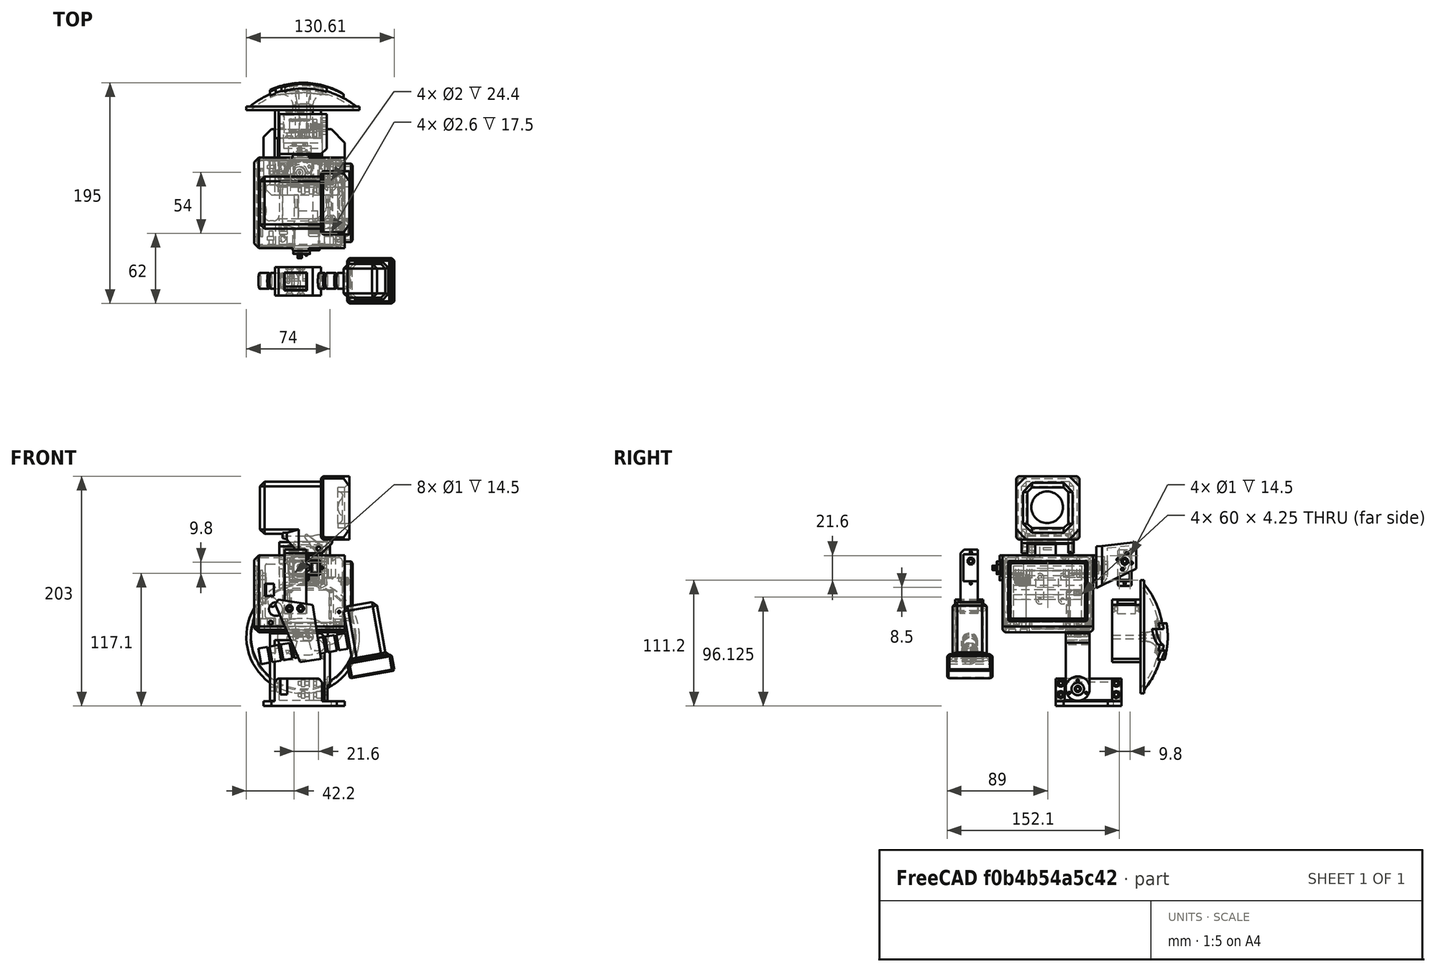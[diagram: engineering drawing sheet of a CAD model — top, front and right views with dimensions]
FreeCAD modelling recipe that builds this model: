
FCSTD DOCUMENT  (FreeCAD 0.16R6348 (Git))
Label: zowi
License: CC-BY 3.0
LicenseURL: http://creativecommons.org/licenses/by/3.0/
objects: Part::Feature×191, Part::Cut×73, Part::Cylinder×67, Part::MultiFuse×58, Part::Box×55, Part::FeaturePython×27, App::DocumentObjectGroup×25, Sketcher::SketchObject×24, Part::Chamfer×21, App::Annotation×20, Part::Fillet×16, PartDesign::Pad×15, Part::Mirroring×13, Part::Part2DObjectPython×11, Part::Sphere×6, PartDesign::Pocket×6, Part::Prism×5, PartDesign::Fillet×3, PartDesign::Chamfer×3, PartDesign::Revolution×3, +3 more types
note: 625 computed .brp shape members not serialized (recipe doc carries the construction recipe); baked Part::Feature solids carry a one-line shape summary decoded from their .brp

FEATURE [Part::Feature] Part__Feature013  label="Servo-D1"
  Placement = pos=(26.5,9.5,100.6) rot=(0,1,0;3.14159rad)
  shape: bbox 55.5 x 20 x 41.74 mm, 365 faces (baked)
FEATURE [Part::Feature] Part__Feature014  label="Servo-D2"
  Placement = pos=(0,0,13) rot=(0.57735,0.57735,0.57735;2.0944rad)
  shape: bbox 41.74 x 55.5 x 20 mm, 365 faces (baked)
FEATURE [Part::Feature] Part__Feature008  label="J1"
  Placement = pos=(-10.8,44.37,77.54) rot=(0.707107,0.707107,0;3.14159rad)
  shape: bbox 11.7 x 15.49 x 2.5 mm, 224 faces (baked)
FEATURE [Part::Feature] Part__Feature009  label="J2"
  Placement = pos=(-10.8,62.15,77.54) rot=(0.707107,0.707107,0;3.14159rad)
  shape: bbox 11.7 x 15.49 x 2.5 mm, 224 faces (baked)
FEATURE [Part::Feature] Part__Feature007  label="J4"
  Placement = pos=(-10.8,59.6199,125.78) rot=(0,0,-1;1.5708rad)
  shape: bbox 11.65 x 20.57 x 2.5 mm, 290 faces (baked)
FEATURE [Part::Feature] Part__Feature010  label="J16"
  Placement = pos=(-9.55,7.19908,100.417) rot=(0.57735,0.57735,-0.57735;2.0944rad)
  shape: bbox 2.94 x 5.43 x 7.98 mm, 414 faces, 0 solids (baked)
FEATURE [Part::Feature] Part__Feature005  label="PCB"
  Placement = pos=(-12.3914,5,75) rot=(0.57735,0.57735,0.57735;2.0944rad)
  shape: bbox 1.591 x 68.6 x 53.36 mm, 426 faces (baked)
FEATURE [Part::Feature] Part__Feature004  label="J010"
  Placement = pos=(-10.8,14.8841,83.3059) rot=(0.707107,0.707107,0;3.14159rad)
  shape: bbox 10.92 x 14.61 x 8.89 mm, 41 faces (baked)
FEATURE [Part::Feature] Part__Feature011  label="U1"
  Placement = pos=(-9.2,12.159,115.511) rot=(0.57735,-0.57735,-0.57735;2.0944rad)
  shape: bbox 2.435 x 26.9 x 13 mm, 503 faces (baked)
FEATURE [Part::Feature] Part__Feature006  label="J8"
  Placement = pos=(-10.8,37.7759,125.78) rot=(0,0,-1;1.5708rad)
  shape: bbox 11.65 x 20.57 x 2.5 mm, 290 faces (baked)
FEATURE [App::DocumentObjectGroup] Group001  label="placa"
  Group = -> [Part__Feature008,Part__Feature009,Part__Feature007,Part__Feature010,Part__Feature005,Part__Feature004,Part__Feature011,Part__Feature006]
FEATURE [Part::Box] Box  label="Cube"
  Height = 24
  Length = 72
  Placement = pos=(-15,-29,-3) rot=(0,0,1;0rad)
  Width = 58
FEATURE [Part::Box] Box001  label="Cube001"
  Height = 25
  Length = 47
  Placement = pos=(-1,-21,2) rot=(0,0,1;0rad)
  Width = 42
FEATURE [Part::Box] Box002  label="Cube002"
  Height = 38
  Length = 28
  Placement = pos=(37,-45,1) rot=(0,0,1;0rad)
  Width = 88
FEATURE [Part::Box] Box003  label="Cube003"
  Height = 38
  Length = 28
  Placement = pos=(-33,-45,1) rot=(0,0,1;0rad)
  Width = 88
FEATURE [Part::Cut] Cut
  Base = -> Box
  Tool = -> Box001
FEATURE [Part::Cut] Cut001
  Base = -> Cut
  Tool = -> Box002
FEATURE [Part::Cut] Cut002
  Base = -> Cut001
  Tool = -> Box003
FEATURE [Part::Box] Box004  label="Cube004"
  Height = 60
  Length = 44
  Placement = pos=(-5,-24,-5) rot=(0,0,1;0rad)
  Width = 61
FEATURE [Part::Mirroring] Part__Mirroring  label="Servo-D1 (Mirror #1)"
  Base = (0,0,0)
  Normal = (0,1,0)
  Placement = pos=(0,72,0) rot=(0,0,1;0rad)
  Source = -> Part__Feature013
FEATURE [Part::Mirroring] Part__Mirroring001  label="Servo-D2 (Mirror #2)"
  Base = (0,0,0)
  Normal = (0,1,0)
  Placement = pos=(0,72,0) rot=(0,0,1;0rad)
  Source = -> Part__Feature014
FEATURE [Part::Cylinder] Cylinder003  label="Joint-D005"
  Angle = 360
  Height = 74.5
  Placement = pos=(-22,9.5,12) rot=(0,1,0;1.5708rad)
  Radius = 1.75
FEATURE [Part::Fillet] Fillet
  Base = -> Cut002
  Edges = 4 edges r=10: [Edge1,Edge3,Edge5,Edge14]
FEATURE [Part::Cylinder] Cylinder002  label="Joint-D004"
  Angle = 360
  Height = 53
  Placement = pos=(-9,9.5,12) rot=(0,1,0;1.5708rad)
  Radius = 10.5
FEATURE [Part::MultiFuse] Fusion
  Shapes = -> [Cylinder002]
FEATURE [Part::Cylinder] Cylinder004  label="Joint-D006"
  Angle = 360
  Height = 74.5
  Placement = pos=(16,9.5,12) rot=(0,1,0;1.5708rad)
  Radius = 5.5
FEATURE [Part::Cut] Cut003
  Base = -> Fusion
  Tool = -> Box004
FEATURE [Part::Cylinder] Cylinder005  label="Joint-D007"
  Angle = 360
  Height = 74.5
  Placement = pos=(-51,9.5,12) rot=(0,1,0;1.5708rad)
  Radius = 1.75
FEATURE [Part::Cut] Cut004
  Base = -> Cut003
  Tool = -> Cylinder004
FEATURE [Part::Cut] Cut005
  Base = -> Cut004
  Tool = -> Cylinder005
FEATURE [Part::Cylinder] Cylinder006  label="Joint-D008"
  Angle = 360
  Height = 74.5
  Placement = pos=(41.8,9.5,12) rot=(0,1,0;1.5708rad)
  Radius = 11
FEATURE [Part::Cut] Cut006
  Base = -> Cut005
  Tool = -> Cylinder006
FEATURE [Part::Cylinder] Cylinder007  label="Joint-D009"
  Angle = 360
  Height = 23.5
  Placement = pos=(16.8,9.5,58.3) rot=(0,1,0;3.14159rad)
  Radius = 11
FEATURE [Part::Cylinder] Cylinder008  label="Joint-D010"
  Angle = 360
  Height = 21.5
  Placement = pos=(16,-24.5,7) rot=(0,1,0;1.5708rad)
  Radius = 1.75
FEATURE [Part::Cylinder] Cylinder009  label="Joint-D011"
  Angle = 360
  Height = 21.5
  Placement = pos=(32,-24.5,7) rot=(0,1,0;1.5708rad)
  Radius = 3
FEATURE [Part::MultiFuse] Fusion001
  Shapes = -> [Cylinder009,Cylinder008]
FEATURE [Part::MultiFuse] Fusion002
  Placement = pos=(0,0,10) rot=(0,0,1;0rad)
  Shapes = -> [Cylinder009,Cylinder008]
FEATURE [Part::MultiFuse] Fusion003
  Placement = pos=(0,49,0) rot=(0,0,1;0rad)
  Shapes = -> [Cylinder009,Cylinder008]
FEATURE [Part::MultiFuse] Fusion004
  Placement = pos=(0,49,10) rot=(0,0,1;0rad)
  Shapes = -> [Cylinder009,Cylinder008]
FEATURE [Part::Box] Box006  label="Cube006"
  Height = 21
  Length = 4
  Placement = pos=(25.5,-28,2) rot=(0,0,1;0rad)
  Width = 56
FEATURE [Part::Cylinder] Cylinder010  label="Joint-D012"
  Angle = 360
  Height = 74.5
  Placement = pos=(17,9.5,12) rot=(0,0,1;0rad)
  Radius = 5.5
FEATURE [Part::Box] Box007  label="Cube007"
  Height = 6
  Length = 3
  Placement = pos=(18.5,-28,4) rot=(0,0,1;0rad)
  Width = 56
FEATURE [Part::Box] Box008  label="Cube008"
  Height = 6
  Length = 3
  Placement = pos=(18.5,-28,14) rot=(0,0,1;0rad)
  Width = 56
FEATURE [Part::Cylinder] Cylinder011  label="Joint-D013"
  Angle = 360
  Height = 74.5
  Placement = pos=(-3,9.5,12) rot=(0,1,0;1.5708rad)
  Radius = 2.75
FEATURE [Part::Box] Box009  label="Cube009"
  Height = 5
  Length = 80
  Placement = pos=(-23,-4,63) rot=(0,0,1;0rad)
  Width = 80
FEATURE [Part::Box] Box010  label="Cube010"
  Height = 9
  Length = 7
  Placement = pos=(-1,-1,63) rot=(0,0,1;0rad)
  Width = 74
FEATURE [Part::Box] Box011  label="Cube011"
  Height = 9
  Length = 7
  Placement = pos=(47,-1,63) rot=(0,0,1;0rad)
  Width = 74
FEATURE [Part::MultiFuse] Fusion005
  Placement = pos=(44,39,98) rot=(0,1,0;1.5708rad)
  Shapes = -> [Cylinder009,Cylinder008]
FEATURE [Part::MultiFuse] Fusion008
  Placement = pos=(44,29,98) rot=(0,1,0;1.5708rad)
  Shapes = -> [Cylinder009,Cylinder008]
FEATURE [Part::MultiFuse] Fusion009
  Placement = pos=(-5,39,98) rot=(0,1,0;1.5708rad)
  Shapes = -> [Cylinder009,Cylinder008]
FEATURE [Part::MultiFuse] Fusion010
  Placement = pos=(-5,29,98) rot=(0,1,0;1.5708rad)
  Shapes = -> [Cylinder009,Cylinder008]
FEATURE [Part::Box] Box012  label="Cube012"
  Height = 9
  Length = 70
  Placement = pos=(-6,8.5,70) rot=(0,0,1;0rad)
  Width = 2
FEATURE [Part::MultiFuse] Fusion011
  Shapes = -> [Box012,Fusion009,Fusion010,Fusion008,Fusion005]
FEATURE [Part::MultiFuse] Fusion012
  Placement = pos=(0,53,0) rot=(0,0,1;0rad)
  Shapes = -> [Box012,Fusion009,Fusion010,Fusion008,Fusion005]
FEATURE [Part::MultiFuse] Fusion013
  Shapes = -> [Box009,Box011,Box010]
FEATURE [Part::Cut] Cut018
  Base = -> Fusion013
  Tool = -> Fusion012
FEATURE [Part::Cut] Cut019
  Base = -> Cut018
  Tool = -> Fusion011
FEATURE [Part::Box] Box014  label="Cube014"
  Height = 43
  Length = 41
  Placement = pos=(6,-1,59) rot=(0,0,1;0rad)
  Width = 21
FEATURE [Part::Box] Box015  label="Cube015"
  Height = 43
  Length = 41
  Placement = pos=(6,52,59) rot=(0,0,1;0rad)
  Width = 21
FEATURE [Part::Cut] Cut020
  Base = -> Cut019
  Tool = -> Box014
FEATURE [Part::Cut] Cut021
  Base = -> Cut020
  Tool = -> Box015
FEATURE [Part::Box] Box016  label="Cube016"
  Height = 12
  Length = 6
  Placement = pos=(-11.5,3,69) rot=(0,0,1;0rad)
  Width = 3
FEATURE [Part::Box] Box017  label="Cube017"
  Height = 12
  Length = 16
  Placement = pos=(-20,-1,63) rot=(0,0,1;0rad)
  Width = 74
FEATURE [Part::Box] Box018  label="Cube018"
  Height = 12
  Length = 6
  Placement = pos=(-11.5,66,69) rot=(0,0,1;0rad)
  Width = 3
FEATURE [Part::MultiFuse] Fusion014
  Shapes = -> [Cut021,Box017]
FEATURE [Part::Cut] Cut022
  Base = -> Fusion014
  Tool = -> Box016
FEATURE [Part::Cut] Cut023
  Base = -> Cut022
  Tool = -> Box018
FEATURE [Part::Box] Box019  label="Cube019"
  Height = 66
  Length = 76
  Placement = pos=(-21,-2,87) rot=(0,0,1;0rad)
  Width = 76
FEATURE [Part::Fillet] Fillet006
  Base = -> Box019
  Edges = 8 edges r=3.5: [Edge1,Edge2,Edge3,Edge5,Edge6,Edge7,Edge10,Edge12]
  Placement = pos=(0,0,-24) rot=(0,0,1;0rad)
FEATURE [Part::Cylinder] Cylinder014  label="Cylinder002"
  Angle = 360
  Height = 31
  Placement = pos=(-8.5,11,71.5) rot=(1,0,0;1.5708rad)
  Radius = 1.75
FEATURE [Part::Cylinder] Cylinder015  label="Cylinder003"
  Angle = 360
  Height = 31
  Placement = pos=(-8.5,80,71.5) rot=(1,0,0;1.5708rad)
  Radius = 1.75
FEATURE [Part::Cylinder] Cylinder016  label="Cylinder004"
  Angle = 360
  Height = 31
  Placement = pos=(-4,11,83.5) rot=(1,0,0;1.5708rad)
  Radius = 6
FEATURE [Part::Box] Box020  label="Cube020"
  Height = 11
  Length = 8
  Placement = pos=(-13.5,-13,95) rot=(0,0,1;0rad)
  Width = 24
FEATURE [PartDesign::Fillet] Fillet011  label="horn"
  Placement = pos=(38.5,9.5,13) rot=(0,0,-1;1.5708rad)
  Radius = 0.5
FEATURE [Part::Cylinder] Cylinder021  label="Joint-D014"
  Angle = 360
  Height = 52.5
  Placement = pos=(19,9.5,20.35) rot=(0,1,0;1.5708rad)
  Radius = 1
FEATURE [Part::Cylinder] Cylinder022  label="Joint-D015"
  Angle = 360
  Height = 52.5
  Placement = pos=(19,2,9.5) rot=(0,1,0;1.5708rad)
  Radius = 1
FEATURE [Part::Cylinder] Cylinder023  label="Joint-D016"
  Angle = 360
  Height = 52.5
  Placement = pos=(19,17,9.5) rot=(0,1,0;1.5708rad)
  Radius = 1
FEATURE [Part::MultiFuse] Fusion017
  Placement = pos=(0,0,-1) rot=(0,0,1;0rad)
  Shapes = -> [Cylinder022,Cylinder021,Cylinder023]
FEATURE [Part::MultiFuse] Fusion018
  Placement = pos=(4,0,101) rot=(0,1,0;1.5708rad)
  Shapes = -> [Cylinder022,Cylinder021,Cylinder023]
FEATURE [PartDesign::Fillet] Fillet012  label="horn001"
  Placement = pos=(16.8,9.5,62.5) rot=(-0.57735,0.57735,-0.57735;2.0944rad)
  Radius = 0.5
FEATURE [Part::Mirroring] Part__Mirroring003  label="horn (Mirror #4)"
  Base = (41.6,1.90735e-06,13)
  Normal = (0,1,-1.19209e-07)
  Placement = pos=(0,72,0) rot=(0,0,1;0rad)
  Source = -> Fillet011
FEATURE [Part::Mirroring] Part__Mirroring004  label="horn001 (Mirror #5)"
  Base = (16.8,7.62939e-06,59.3998)
  Normal = (0,1,-1.19209e-07)
  Placement = pos=(0,72,0) rot=(0,0,1;0rad)
  Source = -> Fillet012
FEATURE [Part::Chamfer] Chamfer
  Base = -> Fillet
  Edges = 3 edges r=3: [Edge18,Edge33,Edge37]
FEATURE [Part::Cut] Cut008
  Base = -> Chamfer
  Tool = -> Cylinder003
FEATURE [Part::Cut] Cut010
  Base = -> Cut008
  Tool = -> Box006
FEATURE [Part::Cut] Cut011
  Base = -> Cut010
  Tool = -> Box008
FEATURE [Part::Cut] Cut012
  Base = -> Cut011
  Tool = -> Box007
FEATURE [Part::Cut] Cut013
  Base = -> Cut012
  Tool = -> Fusion004
FEATURE [Part::Cut] Cut014
  Base = -> Cut013
  Tool = -> Fusion003
FEATURE [Part::Cut] Cut015
  Base = -> Cut014
  Tool = -> Fusion002
FEATURE [Part::Cut] Cut016
  Base = -> Cut015
  Tool = -> Fusion001
FEATURE [Part::Cut] Cut017  label="pie"
  Base = -> Cut016
  Tool = -> Cylinder011
FEATURE [Part::Box] Box024  label="Cube024"
  Height = 23
  Length = 6
  Placement = pos=(0,19,7) rot=(0,0,1;0rad)
  Width = 36
FEATURE [Part::Cut] Cut039  label="pie-D"
  Base = -> Cut017
  Placement = pos=(0,0,1) rot=(0,0,1;0rad)
  Tool = -> Box024
FEATURE [Part::Mirroring] Part__Mirroring006  label="pie-I"
  Base = (0,0,0)
  Normal = (0,1,0)
  Placement = pos=(0,72,0) rot=(0,0,1;0rad)
  Source = -> Cut039
FEATURE [Part::Cut] Cut044
  Base = -> Cut006
  Tool = -> Box004
FEATURE [Part::Cut] Cut045
  Base = -> Cut044
  Tool = -> Cylinder007
FEATURE [Part::Cut] Cut046
  Base = -> Cut045
  Tool = -> Fusion018
FEATURE [Part::Cut] Cut047
  Base = -> Cut046
  Tool = -> Fusion017
FEATURE [Part::Cut] Cut048
  Base = -> Cut047
  Placement = pos=(0,0,1) rot=(0,0,1;0rad)
  Tool = -> Cylinder010
FEATURE [Part::Chamfer] Chamfer001
  Base = -> Cut048
  Edges = 1 edges r=4: [Edge61]
FEATURE [Part::Chamfer] Chamfer002  label="pata-D"
  Base = -> Chamfer001
  Edges = 1 edges r=8: [Edge58]
FEATURE [Part::Mirroring] Part__Mirroring007  label="pata-I"
  Base = (17.5,3.8147e-06,32.25)
  Normal = (0,1,-1.19209e-07)
  Placement = pos=(0,72,0) rot=(0,0,1;0rad)
  Source = -> Chamfer002
FEATURE [Part::Cylinder] Cylinder026  label="Cylinder029"
  Angle = 360
  Height = 31
  Placement = pos=(-7,80,89.6) rot=(1,0,0;1.5708rad)
  Radius = 4
FEATURE [Part::Cylinder] Cylinder012  label="Cylinder030"
  Angle = 360
  Height = 31
  Placement = pos=(-8.5,92,71.5) rot=(1,0,0;1.5708rad)
  Radius = 1.75
FEATURE [Part::Cut] Cut024
  Base = -> Cut023
  Tool = -> Cylinder012
FEATURE [Part::Cylinder] Cylinder013  label="Cylinder001"
  Angle = 360
  Height = 31
  Placement = pos=(-8.5,11,71.5) rot=(1,0,0;1.5708rad)
  Radius = 1.75
FEATURE [Part::Feature] Part__Feature  label="Portapilas008"
  shape: bbox 2e-07 x 47.97 x 51.59 mm, 1 faces, 0 solids (baked)
FEATURE [Part::Feature] Part__Feature015  label="Portapilas007"
  shape: bbox 9.213 x 1.1 x 48.01 mm, 3 faces, 0 solids (baked)
FEATURE [Part::Feature] Part__Feature016  label="Portapilas006"
  shape: bbox 9.213 x 1.1 x 48.01 mm, 3 faces, 0 solids (baked)
FEATURE [Part::Feature] Part__Feature017  label="Portapilas005"
  shape: bbox 9.213 x 1.1 x 48.01 mm, 3 faces, 0 solids (baked)
FEATURE [Part::Feature] Part__Feature018  label="Portapilas004"
  shape: bbox 9.213 x 1.1 x 48.01 mm, 3 faces, 0 solids (baked)
FEATURE [Part::Feature] Part__Feature019  label="Portapilas003"
  shape: bbox 9.213 x 1.1 x 48.01 mm, 3 faces, 0 solids (baked)
FEATURE [Part::Feature] Part__Feature020  label="Portapilas002"
  shape: bbox 9.213 x 1.1 x 48.01 mm, 3 faces, 0 solids (baked)
FEATURE [Part::Feature] Part__Feature021  label="Portapilas001"
  shape: bbox 16.42 x 48.04 x 51.59 mm, 26 faces, 0 solids (baked)
FEATURE [Part::Feature] Part__Feature022  label="Portapilas"
  shape: bbox 21.03 x 69.14 x 72.63 mm, 394 faces, 0 solids (baked)
FEATURE [Part::MultiFuse] Fusion019  label="peterpilas"
  Placement = pos=(23,77.5,76) rot=(0,0,1;1.5708rad)
  Shapes = -> [Part__Feature022,Part__Feature021,Part__Feature020,Part__Feature019,Part__Feature018,Part__Feature017,Part__Feature016,Part__Feature015,Part__Feature]
FEATURE [Part::Feature] Part__Feature023  label="Ultrasonido_BAT"
  Placement = pos=(-17,36,59.5) rot=(0,0,1;0rad)
  shape: bbox 18.72 x 56 x 27.52 mm, 81 faces (baked)
FEATURE [Part::Cylinder] Cylinder027  label="Joint-D019"
  Angle = 360
  Height = 24
  Placement = pos=(16.8,9.5,81) rot=(0,1,0;3.14159rad)
  Radius = 10
FEATURE [Part::Cylinder] Cylinder028  label="Joint-D020"
  Angle = 360
  Height = 24
  Placement = pos=(4.8,9.5,13) rot=(0,1,0;1.5708rad)
  Radius = 10
FEATURE [Part::Mirroring] Part__Mirroring008  label="Joint-D019 (Mirror #7)"
  Base = (0,0,0)
  Normal = (0,1,0)
  Placement = pos=(0,72,0) rot=(0,0,1;0rad)
  Source = -> Cylinder027
FEATURE [Part::Mirroring] Part__Mirroring009  label="Joint-D020 (Mirror #8)"
  Base = (22,1.90735e-06,13)
  Normal = (0,1,-1.19209e-07)
  Placement = pos=(0,72,0) rot=(0,0,1;0rad)
  Source = -> Cylinder028
FEATURE [Part::Box] Box031  label="Cube031"
  Height = 4
  Length = 72
  Placement = pos=(-15,-29,-2) rot=(0,0,1;0rad)
  Width = 58
FEATURE [Part::Fillet] Fillet025
  Base = -> Box031
  Edges = 4 edges r=10: [Edge1,Edge3,Edge5,Edge7]
FEATURE [Part::Mirroring] Part__Mirroring010  label="Fillet025 (Mirror #9)"
  Base = (0,0,0)
  Normal = (0,1,0)
  Placement = pos=(0,72,0) rot=(0,0,1;0rad)
  Source = -> Fillet025
FEATURE [Part::Cylinder] Cylinder034  label="Cylinder082"
  Angle = 360
  Height = 35
  Placement = pos=(51.6,9.5,33) rot=(0.707107,0,-0.707107;3.14159rad)
  Radius = 2.5
FEATURE [Part::Cylinder] Cylinder035  label="Cylinder083"
  Angle = 360
  Height = 20
  Placement = pos=(51.6,9.5,13) rot=(0,0,1;3.14159rad)
  Radius = 2.5
FEATURE [Part::Cylinder] Cylinder036  label="Cylinder084"
  Angle = 360
  Height = 61
  Placement = pos=(-9.4,9.5,13) rot=(0.707107,0,0.707107;3.14159rad)
  Radius = 2.5
FEATURE [Part::Sphere] Sphere
  Angle1 = -90
  Angle2 = 90
  Angle3 = 360
  Placement = pos=(16.8,9.5,33) rot=(1,0,0;3.14159rad)
  Radius = 2.5
FEATURE [Part::Sphere] Sphere008
  Angle1 = -90
  Angle2 = 90
  Angle3 = 360
  Placement = pos=(51.6,9.5,33) rot=(0.707107,0,-0.707107;3.14159rad)
  Radius = 2.5
FEATURE [Part::Cylinder] Cylinder037  label="Cylinder085"
  Angle = 360
  Height = 11
  Placement = pos=(-9.4,9.5,2) rot=(0,0,1;3.14159rad)
  Radius = 2.5
FEATURE [Part::Sphere] Sphere009
  Angle1 = -90
  Angle2 = 90
  Angle3 = 360
  Placement = pos=(51.6,9.5,13) rot=(0.707107,0,-0.707107;3.14159rad)
  Radius = 2.5
FEATURE [Part::Cylinder] Cylinder038  label="cylinder001"
  Angle = 360
  Height = 83
  Placement = pos=(16.8,9.5,33) rot=(0,0,1;3.14159rad)
  Radius = 2.5
FEATURE [Part::Sphere] Sphere010
  Angle1 = -90
  Angle2 = 90
  Angle3 = 360
  Placement = pos=(16.8,9.5,116) rot=(1,0,0;3.14159rad)
  Radius = 2.5
FEATURE [Part::Sphere] Sphere011
  Angle1 = -90
  Angle2 = 90
  Angle3 = 360
  Placement = pos=(-9.4,9.5,2) rot=(0.707107,0,-0.707107;3.14159rad)
  Radius = 2.5
FEATURE [Part::Sphere] Sphere012
  Angle1 = -90
  Angle2 = 90
  Angle3 = 360
  Placement = pos=(-9.4,9.5,13) rot=(0.707107,0,-0.707107;3.14159rad)
  Radius = 2.5
FEATURE [Part::Cylinder] Cylinder039  label="Cylinder086"
  Angle = 360
  Height = 53
  Placement = pos=(16.8,9.5,116) rot=(-1,0,0;1.5708rad)
  Radius = 2.5
FEATURE [Part::MultiFuse] Fusion021
  Placement = pos=(0,53,0) rot=(0,0,1;0rad)
  Shapes = -> [Cylinder037,Cylinder036,Sphere012,Cylinder035,Cylinder034,Cylinder038,Sphere010,Sphere008,Sphere009,Sphere,Sphere011]
FEATURE [Part::MultiFuse] Fusion022
  Shapes = -> [Cylinder037,Cylinder036,Sphere012,Cylinder035,Cylinder034,Cylinder038,Sphere010,Sphere008,Sphere009,Sphere,Sphere011]
FEATURE [App::DocumentObjectGroup] Group  label="kinematic"
  Group = -> [Cylinder039,Part__Mirroring008,Cylinder027,Fusion021,Fusion022,Cylinder028,Part__Mirroring009,Part__Mirroring010,Fillet025]
FEATURE [Part::Cut] Cut050
  Base = -> Cut024
  Tool = -> Cylinder013
FEATURE [Part::Box] Box032  label="Cube032"
  Height = 25
  Length = 55
  Placement = pos=(-1,20,66) rot=(0,0,1;0rad)
  Width = 32
FEATURE [Part::Box] Box033  label="Cube033"
  Height = 54
  Length = 4.5
  Placement = pos=(-20,6,64) rot=(0,0,1;0rad)
  Width = 60
FEATURE [Part::Box] Box035  label="Cube035"
  Height = 68
  Length = 6
  Placement = pos=(-23.5,17,68) rot=(0,0,1;0rad)
  Width = 38
FEATURE [Part::Box] Box036  label="Cube034"
  Height = 17
  Length = 13
  Placement = pos=(-14,20,62) rot=(0,0,1;0rad)
  Width = 32
FEATURE [Part::Fillet] Fillet018002
  Base = -> Box036
  Edges = 4 edges r=5: [Edge1,Edge3,Edge5,Edge7]
FEATURE [Part::Cylinder] Cylinder  label="Cylinder087"
  Angle = 360
  Height = 31
  Placement = pos=(-49.5,29,111.5) rot=(0,1,0;1.5708rad)
  Radius = 1.75
FEATURE [Part::Cylinder] Cylinder040  label="Cylinder088"
  Angle = 360
  Height = 31
  Placement = pos=(-49.5,49,91.5) rot=(0,1,0;1.5708rad)
  Radius = 1.75
FEATURE [Part::Cylinder] Cylinder041  label="Cylinder089"
  Angle = 360
  Height = 31
  Placement = pos=(-49.5,49,111.5) rot=(0,1,0;1.5708rad)
  Radius = 1.75
FEATURE [Part::MultiFuse] Fusion025
  Shapes = -> [Box032,Cut050]
FEATURE [Part::Box] Box037  label="Cube036"
  Height = 44
  Length = 61
  Placement = pos=(-9,22,66) rot=(0,0,1;0rad)
  Width = 28
FEATURE [Part::MultiFuse] Fusion026
  Shapes = -> [Fusion025,Box033]
FEATURE [Part::Cut] Cut051
  Base = -> Fusion026
  Tool = -> Fillet018002
FEATURE [Part::Box] Box038  label="Cube037"
  Height = 11
  Length = 8
  Placement = pos=(-11.5,-52,95) rot=(0,0,1;0rad)
  Width = 58
FEATURE [Part::Cylinder] Cylinder042  label="Cylinder090"
  Angle = 360
  Height = 61
  Placement = pos=(-5,124,89.6) rot=(1,0,0;1.5708rad)
  Radius = 4
FEATURE [Part::Cylinder] Cylinder043  label="Cylinder091"
  Angle = 360
  Height = 63
  Placement = pos=(-3,11,83.5) rot=(1,0,0;1.5708rad)
  Radius = 6
FEATURE [Part::Box] Box039  label="Cube038"
  Height = 66
  Length = 76
  Placement = pos=(-21,-2,63) rot=(0,0,1;0rad)
  Width = 76
FEATURE [Part::Cylinder] Cylinder044  label="Cylinder092"
  Angle = 360
  Height = 23
  Placement = pos=(-8.5,1,71.5) rot=(1,0,0;1.5708rad)
  Radius = 1.75
FEATURE [Part::Cylinder] Cylinder045  label="Cylinder093"
  Angle = 360
  Height = 31
  Placement = pos=(-8.5,94,71.5) rot=(1,0,0;1.5708rad)
  Radius = 1.75
FEATURE [Part::Fillet] Fillet018007
  Base = -> Box039
  Edges = 8 edges r=3: [Edge1,Edge2,Edge3,Edge5,Edge6,Edge7,Edge10,Edge12]
FEATURE [Part::Box] Box040  label="Cube039"
  Height = 6
  Length = 81
  Placement = pos=(-23.5,-4.5,63) rot=(0,0,1;0rad)
  Width = 81
FEATURE [Part::Fillet] Fillet018008
  Base = -> Box040
  Edges = 4 edges r=5: [Edge1,Edge3,Edge5,Edge7]
  Placement = pos=(0,0,-1) rot=(0,0,1;0rad)
FEATURE [Part::Cylinder] Cylinder046  label="Cylinder094"
  Angle = 360
  Height = 45
  Placement = pos=(-8.5,-7,71.5) rot=(1,0,0;1.5708rad)
  Radius = 4
FEATURE [Part::Cylinder] Cylinder047  label="Cylinder095"
  Angle = 360
  Height = 45
  Placement = pos=(-8.5,124,71.5) rot=(1,0,0;1.5708rad)
  Radius = 4
FEATURE [Part::MultiFuse] Fusion033
  Shapes = -> [Fillet018007,Fillet018008]
FEATURE [Part::MultiFuse] Fusion034  label="corte-positivo"
  Shapes = -> [Fusion033,Cylinder042,Cylinder047,Cylinder045,Cylinder046,Cylinder043,Box038,Cylinder044]
FEATURE [Part::Feature] hull002
  shape: bbox 10 x 17.12 x 30.33 mm, 240 faces (baked)
FEATURE [Part::Box] Box042  label="Cube041"
  Height = 23
  Length = 6
  Placement = pos=(0,19,7) rot=(0,0,1;0rad)
  Width = 36
FEATURE [Part::Cut] Cut060  label="pie001"
  Base = -> Cut016
  Tool = -> Cylinder011
FEATURE [Part::Cut] Cut059  label="piepatin"
  Base = -> Cut060
  Placement = pos=(0,0,1) rot=(0,0,1;0rad)
  Tool = -> Box042
FEATURE [Part::Cylinder] Cylinder052  label="Cylinder096"
  Angle = 360
  Height = 27
  Placement = pos=(8,-25,17) rot=(1,0,0;1.0472rad)
  Radius = 1.75
FEATURE [Part::MultiFuse] Fusion035
  Shapes = -> [hull002,Cut059]
FEATURE [Part::Prism] prism
  Circumradius = 3.5
  Height = 10
  Placement = pos=(8,-17,12.375) rot=(1,0,0;1.0472rad)
  Polygon = 6
FEATURE [Part::MultiFuse] Fusion036
  Shapes = -> [Cylinder052,prism]
FEATURE [Part::Cut] Cut061  label="patin"
  Base = -> Fusion035
  Tool = -> Fusion036
FEATURE [Part::Box] Box044  label="Cube043"
  Height = 30
  Length = 3
  Placement = pos=(-26,16,70) rot=(0,0,1;0rad)
  Width = 40
FEATURE [Part::Feature] Cut062
  Placement = pos=(-82.5,-7.75,37) rot=(0,1,0;3.14159rad)
  shape: bbox 20 x 20 x 38.5 mm, 2097 faces (baked)
FEATURE [Part::Feature] hull003
  shape: bbox 48 x 3 x 83 mm, 8 faces (baked)
FEATURE [Part::MultiFuse] Fusion037  label="cola"
  Shapes = -> [Box044,hull003,Cut062]
FEATURE [App::DocumentObjectGroup] Group002  label="patines"
  Group = -> [Cut061,Fusion037]
FEATURE [Part::Cylinder] Cylinder053  label="Cylinder097"
  Angle = 360
  Height = 31
  Placement = pos=(-49.5,29,91.5) rot=(0,1,0;1.5708rad)
  Radius = 1.75
FEATURE [Part::MultiFuse] Fusion038
  Placement = pos=(14,0,0) rot=(0,0,1;0rad)
  Shapes = -> [Cylinder053,Cylinder040,Cylinder041,Cylinder]
FEATURE [App::DocumentObjectGroup] Group004  label="electronic"
  Group = -> [Part__Mirroring,Part__Mirroring001,Part__Mirroring003,Part__Mirroring004,Fusion019,Part__Feature023,Group001]
FEATURE [App::DocumentObjectGroup] Group005  label="aux"
  Group = -> [Fusion034]
FEATURE [App::DocumentObjectGroup] Group003  label="original-src"
  Group = -> [Part__Mirroring006,Part__Mirroring007,Group004,Group005]
FEATURE [Part::Cut] Cut066
  Base = -> Cut051
  Tool = -> Box037
FEATURE [Part::Chamfer] Chamfer003
  Base = -> Cut066
  Edges = 1 edges r=3: [Edge1]
FEATURE [Sketcher::SketchObject] Sketch
  Placement = pos=(-22,0,0) rot=(0.57735,-0.57735,-0.57735;2.0944rad)
  sketch-geometry (4):
    g0: ArcOfCircle CenterX=-49 CenterY=111.5 CenterZ=0 NormalX=0 NormalY=0 NormalZ=1 Radius=3.5 StartAngle=9.1497e-08 EndAngle=3.14159
    g1: LineSegment StartX=-52.5 StartY=111.5 StartZ=0 EndX=-52.5 EndY=91.5 EndZ=0
    g2: LineSegment StartX=-45.5 StartY=111.5 StartZ=0 EndX=-45.5 EndY=91.5 EndZ=0
    g3: ArcOfCircle CenterX=-49 CenterY=91.5 CenterZ=0 NormalX=0 NormalY=0 NormalZ=1 Radius=3.5 StartAngle=3.14159 EndAngle=6.28319
  constraints (13):
    c: DistanceX(g-1,g0) = -49
    c: DistanceY(g-1,g0) = 111.5
    c: Radius(g0) = 3.5
    c: Vertical(g1)
    c: Vertical(g2)
    c: Coincident(g1,g0)
    c: Coincident(g2,g0)
    c: Tangent(g2,g0)
    c: Tangent(g1,g0)
    c: Coincident(g3,g1)
    c: Coincident(g3,g2)
    c: Equal(g3,g0)
    c: Distance(g3,g0) = 20
FEATURE [PartDesign::Pad] Pad
  Length = 5
  Length2 = 100
  Placement = pos=(-22,0,0) rot=(0.57735,-0.57735,-0.57735;2.0944rad)
  Reversed = true
  Sketch = -> Sketch
  Type = 0
FEATURE [Part::FeaturePython] Clone  label="Clone of Pad"  # Draft clone (typed FeaturePython)
  Objects = -> [Pad]
  Placement = pos=(-22,-20,0) rot=(0.57735,-0.57735,-0.57735;2.0944rad)
  Scale = (1,1,1)
FEATURE [Part::MultiFuse] Fusion039
  Placement = pos=(4.5,0,0) rot=(0,0,1;0rad)
  Shapes = -> [Pad,Clone]
FEATURE [Part::MultiFuse] Fusion040
  Shapes = -> [Chamfer003,Fusion039]
FEATURE [Part::Cut] Cut067
  Base = -> Fusion040
  Tool = -> Fusion038
FEATURE [Part::Cut] Cut068
  Base = -> Cut067
  Tool = -> Box035
FEATURE [Part::Box] Box047  label="Cube046"
  Height = 49
  Length = 17
  Placement = pos=(-14,-2.5,75) rot=(0,0,1;0rad)
  Width = 77
FEATURE [Part::Fillet] Fillet018014
  Base = -> Box047
  Edges = 12 edges r=2: [Edge1,Edge2,Edge3,Edge4,Edge5,Edge6,Edge7,Edge8,Edge9,Edge10,Edge11,Edge12]
FEATURE [Part::Feature] Part__Mirroring007001  label="pata-orig"
  Placement = pos=(-17,-62,-9.49999) rot=(-1,0,0;1.5708rad)
  shape: bbox 53 x 59.5 x 21 mm, 32 faces (baked)
FEATURE [Sketcher::SketchObject] Sketch001  label="leg-sketch-1"
  Placement = pos=(0,0,0) rot=(0.57735,0.57735,0.57735;2.0944rad)
  sketch-geometry (5):
    g0: LineSegment StartX=-49 StartY=10.5 StartZ=0 EndX=0 EndY=10.5 EndZ=0
    g1: LineSegment StartX=0 StartY=10.5 StartZ=0 EndX=0 EndY=-10.5 EndZ=0
    g2: LineSegment StartX=0 StartY=-10.5 StartZ=0 EndX=-49 EndY=-10.5 EndZ=0
    g3: LineSegment [constr] StartX=-49 StartY=-10.5 StartZ=0 EndX=-49 EndY=10.5 EndZ=0
    g4: ArcOfCircle CenterX=-49 CenterY=0 CenterZ=0 NormalX=0 NormalY=0 NormalZ=1 Radius=10.5 StartAngle=1.5708 EndAngle=4.71239
  constraints (15):
    c: Coincident(g0,g1)
    c: Coincident(g1,g2)
    c: Coincident(g2,g3)
    c: Coincident(g3,g0)
    c: Horizontal(g0)
    c: Horizontal(g2)
    c: Vertical(g1)
    c: Vertical(g3)
    c: PointOnObject(g4,g3)
    c: Coincident(g4,g0)
    c: Coincident(g4,g2)
    c: PointOnObject(g4,g-1)
    c: PointOnObject(g0,g-2)
    c: DistanceX(g0) = 49
    c: DistanceY(g1) = -21
FEATURE [PartDesign::Pad] Pad001  label="leg-block-1"
  Length = 53
  Length2 = 100
  Midplane = true
  Placement = pos=(0,0,0) rot=(0.57735,0.57735,0.57735;2.0944rad)
  Sketch = -> Sketch001
  Type = 0
FEATURE [Sketcher::SketchObject] Sketch002  label="leg-top-sketch"
  ExternalGeometry = -> [Pad001]
  Placement = pos=(0,0,10.5) rot=(0,0,-1;1.5708rad)
  Support = -> Pad001 [Face1]
  sketch-geometry (9):
    g0: LineSegment StartX=64 StartY=21.5 StartZ=0 EndX=10 EndY=21.5 EndZ=0
    g1: LineSegment StartX=6 StartY=17.5 StartZ=0 EndX=6 EndY=-19.5 EndZ=0
    g2: LineSegment StartX=9 StartY=-22.5 StartZ=0 EndX=64 EndY=-22.5 EndZ=0
    g3: LineSegment StartX=64 StartY=-22.5 StartZ=0 EndX=64 EndY=21.5 EndZ=0
    g4: LineSegment StartX=6 StartY=17.5 StartZ=0 EndX=10 EndY=21.5 EndZ=0
    g5: LineSegment [constr] StartX=6 StartY=17.5 StartZ=0 EndX=6 EndY=21.5 EndZ=0
    g6: LineSegment StartX=6 StartY=-19.5 StartZ=0 EndX=9 EndY=-22.5 EndZ=0
    g7: LineSegment [constr] StartX=9 StartY=-22.5 StartZ=0 EndX=6 EndY=-22.5 EndZ=0
    g8: LineSegment [constr] StartX=6 StartY=-22.5 StartZ=0 EndX=6 EndY=-19.5 EndZ=0
  constraints (26):
    c: Coincident(g2,g3)
    c: Coincident(g3,g0)
    c: Horizontal(g0)
    c: Horizontal(g2)
    c: Vertical(g1)
    c: Vertical(g3)
    c: DistanceY(g-3,g5) = -5
    c: DistanceY(g7,g-4) = -4
    c: Angle(g-2,g4) = 2.35619
    c: Coincident(g1,g4)
    c: Coincident(g5,g1)
    c: Vertical(g5)
    c: DistanceY(g1,g7) = -40
    c: DistanceX(g5,g-3) = -6
    c: Coincident(g0,g4)
    c: PointOnObject(g5,g0)
    c: DistanceX(g-3,g0) = 15
    c: Coincident(g2,g6)
    c: Coincident(g7,g2)
    c: Horizontal(g7)
    c: DistanceX(g7) = -3
    c: Coincident(g1,g6)
    c: Coincident(g8,g7)
    c: Coincident(g8,g1)
    c: Equal(g8,g7)
    c: Vertical(g8)
FEATURE [PartDesign::Pocket] Pocket  label="leg-block-2"
  Length = 5
  Placement = pos=(0,0,0) rot=(0.57735,0.57735,0.57735;2.0944rad)
  Sketch = -> Sketch002
  Type = 1
FEATURE [Sketcher::SketchObject] Sketch003  label="ankle-rounded-horn-sketch"
  ExternalGeometry = -> [Pocket]
  Placement = pos=(26.5,0,0) rot=(0.57735,0.57735,0.57735;2.0944rad)
  Support = -> Pocket [Face4]
  sketch-geometry (1):
    g0: Circle CenterX=-49 CenterY=0 CenterZ=0 NormalX=0 NormalY=0 NormalZ=1 Radius=10.75
  constraints (2):
    c: Coincident(g0,g-3)
    c: Radius(g0) = 10.75
FEATURE [PartDesign::Pocket] Pocket001  label="ankle-rounded-horn-cutout"
  Length = 2.2
  Placement = pos=(0,0,0) rot=(0.57735,0.57735,0.57735;2.0944rad)
  Sketch = -> Sketch003
  Type = 0
FEATURE [Sketcher::SketchObject] Sketch004  label="ankle-rear-shaft-drill-sketch"
  ExternalGeometry = -> [Pocket001]
  Placement = pos=(-26.5,0,0) rot=(0.57735,0.57735,-0.57735;4.18879rad)
  Support = -> Pocket001 [Face2]
  sketch-geometry (1):
    g0: Circle CenterX=-49 CenterY=0 CenterZ=0 NormalX=0 NormalY=0 NormalZ=1 Radius=1.75
  constraints (2):
    c: Coincident(g0,g-3)
    c: Radius(g0) = 1.75
FEATURE [PartDesign::Pocket] Pocket002  label="ankle-rear-shaft-drill"
  Length = 0
  Placement = pos=(0,0,0) rot=(0.57735,0.57735,0.57735;2.0944rad)
  Sketch = -> Sketch004
  Type = 2
FEATURE [Sketcher::SketchObject] Sketch005  label="hip-rounded-horn-cutout-sketch"
  Placement = pos=(0,-6,0) rot=(-0.57735,-0.57735,0.57735;4.18879rad)
  Support = -> Pocket002 [Face10]
  sketch-geometry (1):
    g0: Circle CenterX=0 CenterY=0 CenterZ=0 NormalX=0 NormalY=0 NormalZ=1 Radius=11
  constraints (2):
    c: Coincident(g0,g-1)
    c: Radius(g0) = 11
FEATURE [PartDesign::Pocket] Pocket003  label="hip-rounded-horn-cutout"
  Length = 3.3
  Placement = pos=(0,0,0) rot=(0.57735,0.57735,0.57735;2.0944rad)
  Sketch = -> Sketch005
  Type = 0
FEATURE [Sketcher::SketchObject] Sketch006  label="horn-side-chamfer-sketch"
  ExternalGeometry = -> [Pocket003]
  Placement = pos=(0,0,10.5) rot=(0,0,-1;1.5708rad)
  Support = -> Pocket003 [Face1]
  sketch-geometry (3):
    g0: LineSegment StartX=0 StartY=18.5 StartZ=0 EndX=8 EndY=26.5 EndZ=0
    g1: LineSegment StartX=0 StartY=18.5 StartZ=0 EndX=0 EndY=26.5 EndZ=0
    g2: LineSegment StartX=0 StartY=26.5 StartZ=0 EndX=8 EndY=26.5 EndZ=0
  constraints (8):
    c: PointOnObject(g0,g-2)
    c: PointOnObject(g0,g-3)
    c: Angle(g-2,g0) = 2.35619
    c: DistanceY(g-3,g0) = -8
    c: Coincident(g0,g1)
    c: Coincident(g1,g-3)
    c: Coincident(g1,g2)
    c: Coincident(g2,g0)
FEATURE [PartDesign::Pocket] Pocket004  label="horn-side-chamfer"
  Length = 5
  Placement = pos=(0,0,0) rot=(0.57735,0.57735,0.57735;2.0944rad)
  Sketch = -> Sketch006
  Type = 1
FEATURE [Part::Cylinder] Cylinder054  label="servo-shaft-drill"
  Angle = 360
  Height = 20
  Placement = pos=(0,10,0) rot=(1,0,0;1.5708rad)
  Radius = 5.5
FEATURE [Part::Cylinder] Cylinder055  label="servo-horn-small-drill-master"
  Angle = 360
  Height = 20
  Placement = pos=(-3.5,10,7.5) rot=(1,0,0;1.5708rad)
  Radius = 1
FEATURE [Part::FeaturePython] Clone001  label="Clone of servo-horn-small-drill-master"  # Draft clone (typed FeaturePython)
  Objects = -> [Cylinder055]
  Placement = pos=(7.35,10,-2.33815e-06) rot=(1,0,0;1.5708rad)
  Scale = (1,1,1)
FEATURE [Part::FeaturePython] Clone002  label="Clone of servo-horn-small-drill-master001"  # Draft clone (typed FeaturePython)
  Objects = -> [Cylinder055]
  Placement = pos=(-3.5,10,-7.5) rot=(1,0,0;1.5708rad)
  Scale = (1,1,1)
FEATURE [Part::MultiFuse] Fusion041  label="servo-Drills-block1-master"
  Shapes = -> [Clone001,Clone002,Cylinder055,Cylinder054]
FEATURE [Part::FeaturePython] Clone003  label="Clone of servo-Drills-block1-master"  # Draft clone (typed FeaturePython)
  Objects = -> [Fusion041]
  Placement = pos=(22,-49,6.96015e-06) rot=(0,0,1;1.5708rad)
  Scale = (1,1,1)
FEATURE [Part::MultiFuse] Fusion042  label="Servo-horn-drills"
  Shapes = -> [Fusion041,Clone003]
FEATURE [Part::Cut] Cut070  label="Leg"
  Base = -> Pocket004
  Tool = -> Fusion042
FEATURE [App::DocumentObjectGroup] Group007  label="Leg-src"
  Group = -> [Pad001,Pocket,Pocket001,Pocket002,Pocket003,Cut070]
FEATURE [Sketcher::SketchObject] Sketch007
  sketch-geometry (15):
    g0: LineSegment StartX=-15.86 StartY=-10 StartZ=0 EndX=15.86 EndY=-10 EndZ=0
    g1: ArcOfCircle CenterX=-25 CenterY=0 CenterZ=0 NormalX=0 NormalY=0 NormalZ=1 Radius=3.00012 StartAngle=0.897592 EndAngle=5.38559
    g2: ArcOfCircle CenterX=25 CenterY=0 CenterZ=0 NormalX=0 NormalY=0 NormalZ=1 Radius=3.00012 StartAngle=4.03918 EndAngle=8.52719
    g3: Circle CenterX=-25 CenterY=0 CenterZ=0 NormalX=0 NormalY=0 NormalZ=1 Radius=1.6
    g4: Circle CenterX=25 CenterY=0 CenterZ=0 NormalX=0 NormalY=0 NormalZ=1 Radius=1.6
    g5: LineSegment [constr] StartX=-25 StartY=31.675 StartZ=0 EndX=25 EndY=31.675 EndZ=0
    g6: LineSegment [constr] StartX=-25 StartY=31.675 StartZ=0 EndX=-25 EndY=0 EndZ=0
    g7: LineSegment [constr] StartX=3.61551 StartY=10 StartZ=0 EndX=3.61551 EndY=-10 EndZ=0
    g8: LineSegment StartX=-15.86 StartY=10 StartZ=0 EndX=15.86 EndY=10 EndZ=0
    g9: ArcOfCircle CenterX=-15.6958 CenterY=2.56491 CenterZ=0 NormalX=0 NormalY=0 NormalZ=1 Radius=7.4369 StartAngle=1.59288 EndAngle=3.17109
    g10: ArcOfCircle CenterX=-15.6958 CenterY=-2.56491 CenterZ=0 NormalX=0 NormalY=0 NormalZ=1 Radius=7.4369 StartAngle=3.11209 EndAngle=4.69031
    g11: ArcOfCircle CenterX=15.6958 CenterY=2.56491 CenterZ=0 NormalX=0 NormalY=0 NormalZ=1 Radius=7.4369 StartAngle=6.25369 EndAngle=7.8319
    g12: ArcOfCircle CenterX=15.6958 CenterY=-2.56491 CenterZ=0 NormalX=0 NormalY=0 NormalZ=1 Radius=7.4369 StartAngle=4.73447 EndAngle=6.31268
    g13: LineSegment [constr] StartX=-28.0001 StartY=-22.7357 StartZ=0 EndX=27.9999 EndY=-22.7357 EndZ=0
    g14: LineSegment [constr] StartX=-28.0001 StartY=1.36738e-07 StartZ=0 EndX=-28.0001 EndY=-22.7357 EndZ=0
  constraints (43):
    c: Coincident(g3,g1)
    c: Coincident(g4,g2)
    c: Horizontal(g5)
    c: DistanceX(g5) = 50
    c: Coincident(g6,g5)
    c: Vertical(g6)
    c: Coincident(g1,g6)
    c: DistanceY(g7) = -20
    c: Symmetric(g7,g7,g-1)
    c: Symmetric(g8,g0,g-1)
    c: Equal(g8,g0)
    c: Equal(g2,g1)
    c: Radius(g3) = 1.6
    c: Coincident(g9,g1)
    c: Coincident(g8,g9)
    c: Equal(g4,g3)
    c: Symmetric(g2,g1,g-2)
    c: Symmetric(g2,g1,g-2)
    c: Coincident(g11,g8)
    c: Coincident(g0,g12)
    c: Coincident(g10,g0)
    c: Coincident(g10,g1)
    c: Coincident(g12,g2)
    c: Horizontal(g8)
    c: Horizontal(g0)
    c: PointOnObject(g7,g8)
    c: DistanceX(g8) = 31.72
    c: PointOnObject(g1,g-1)
    c: Symmetric(g8,g8,g-2)
    c: Horizontal(g13)
    c: DistanceX(g13) = 56
    c: PointOnObject(g14,g1)
    c: Coincident(g14,g13)
    c: Vertical(g14)
    c: Tangent(g14,g1)
    c: Equal(g9,g11)
    c: Equal(g12,g11)
    c: Equal(g10,g9)
    c: Coincident(g11,g2)
    c: Symmetric(g5,g5,g-2)
    c: Symmetric(g2,g2,g-1)
    c: Symmetric(g1,g1,g-1)
    c: Symmetric(g2,g1,g-2)
FEATURE [PartDesign::Pad] Pad002
  Length = 1.68
  Length2 = 100
  Sketch = -> Sketch007
  Type = 0
FEATURE [Sketcher::SketchObject] Sketch008
  ExternalGeometry = -> [Pad002]
  Placement = pos=(0,0,1.68) rot=(0,0,1;0rad)
  Support = -> Pad002 [Face12]
  sketch-geometry (3):
    g0: Circle CenterX=-14 CenterY=0 CenterZ=0 NormalX=0 NormalY=0 NormalZ=1 Radius=7.8
    g1: Circle CenterX=14 CenterY=0 CenterZ=0 NormalX=0 NormalY=0 NormalZ=1 Radius=7.8
    g2: LineSegment [constr] StartX=-25 StartY=0 StartZ=0 EndX=-14 EndY=0 EndZ=0
  constraints (10):
    c: PointOnObject(g0,g-1)
    c: PointOnObject(g1,g-1)
    c: Symmetric(g0,g1,g-2)
    c: Equal(g0,g1)
    c: Radius(g1) = 7.8
    c: Coincident(g2,g-3)
    c: Coincident(g2,g0)
    c: Horizontal(g2)
    c: Tangent(g2,g-1)
    c: DistanceX(g2) = 11
FEATURE [PartDesign::Pad] Pad003
  Length = 12
  Length2 = 100
  Sketch = -> Sketch008
  Type = 0
FEATURE [PartDesign::Chamfer] Chamfer005
  Base = -> Pad003 [Edge34,Edge36]
  Size = 0.3
FEATURE [App::DocumentObjectGroup] Group008  label="fake-ultrasound"
  Group = -> [Pad002,Pad003,Chamfer005]
FEATURE [App::DocumentObjectGroup] Group006  label="src"
  Group = -> [Group007,Part__Mirroring007001,Group008]
FEATURE [Part::Feature] Part__Mirroring007002  label="pie-I001"
  Placement = pos=(-202.95,69.39,2) rot=(0,0,-1;1.5708rad)
  shape: bbox 58 x 72 x 24 mm, 84 faces (baked)
FEATURE [Part::Feature] Cut071  label="pie-D001"
  Placement = pos=(-274.85,69.19,3) rot=(0,0,-1;1.5708rad)
  shape: bbox 58 x 72 x 24 mm, 84 faces (baked)
FEATURE [Part::Feature] Part__Mirroring007003  label="pata-I001"
  Placement = pos=(-202.95,69.9,1.95) rot=(0,0,-1;1.5708rad)
  shape: bbox 21 x 53 x 59.5 mm, 32 faces (baked)
FEATURE [Part::Feature] Chamfer006  label="chasis001"
  Placement = pos=(-275,70,2.44) rot=(0,0,-1;1.5708rad)
  shape: bbox 80 x 80 x 55 mm, 159 faces (baked)
FEATURE [Part::Feature] Cut072  label="head001"
  Placement = pos=(-275,70,2.44) rot=(0,0,-1;1.5708rad)
  shape: bbox 80 x 80 x 63 mm, 68 faces (baked)
FEATURE [Part::Feature] Part__Mirroring007004  label="leg-body"
  Placement = pos=(-255.95,69.7,1.95) rot=(0,0,-1;1.5708rad)
  shape: bbox 21 x 53 x 59.5 mm, 32 faces (baked)
FEATURE [Part::Feature] Chamfer007  label="ISO-10642-M3x10"
  Placement = pos=(-265.35,70.0132,15) rot=(0.57735,0.57735,-0.57735;2.0944rad)
  shape: bbox 6.046 x 10 x 6.046 mm, 25 faces (baked)
FEATURE [Part::Feature] Chamfer008  label="ISO-10642-M3x011"
  Placement = pos=(-212.45,70.2132,15) rot=(0.57735,0.57735,-0.57735;2.0944rad)
  shape: bbox 6.046 x 10 x 6.046 mm, 25 faces (baked)
FEATURE [Part::Feature] Chamfer009  label="ISO4032-Hex-Nut-M3"
  Placement = pos=(-250.35,48.29,20) rot=(0,0,1;0rad)
  shape: bbox 6.35 x 2.4 x 6.35 mm, 29 faces (baked)
FEATURE [Part::Feature] Chamfer010  label="ISO4032-Hex-Nut-M004"
  Placement = pos=(-250.35,47.69,10) rot=(0,0,1;0rad)
  shape: bbox 6.35 x 2.4 x 6.35 mm, 29 faces (baked)
FEATURE [Part::Feature] Chamfer011  label="ISO4032-Hex-Nut-M005"
  Placement = pos=(-299.35,47.69,20) rot=(0,0,1;0rad)
  shape: bbox 6.35 x 2.4 x 6.35 mm, 29 faces (baked)
FEATURE [Part::Feature] Chamfer012  label="ISO4032-Hex-Nut-M006"
  Placement = pos=(-299.35,47.69,10) rot=(0,0,1;0rad)
  shape: bbox 6.35 x 2.4 x 6.35 mm, 29 faces (baked)
FEATURE [Part::Feature] Chamfer013  label="ISO4762_Hex_screw-M3x16"
  Placement = pos=(-299.35,37.19,20) rot=(0.57735,0.57735,-0.57735;2.0944rad)
  shape: bbox 5.5 x 19 x 5.5 mm, 16 faces (baked)
FEATURE [Part::Feature] Compound  label="Servo-Futaba-3003-ready001"
  Placement = pos=(-274.9,69.49,14.95) rot=(1,0,0;1.5708rad)
  shape: bbox 57.75 x 41.74 x 20 mm, 378 faces, 4 solids (baked)
FEATURE [Part::Feature] Chamfer014  label="ISO4762_Hex_screw-M3x017"
  Placement = pos=(-299.35,37.29,10) rot=(0.57735,0.57735,-0.57735;2.0944rad)
  shape: bbox 5.5 x 19 x 5.5 mm, 16 faces (baked)
FEATURE [Part::Feature] Chamfer015  label="ISO4762_Hex_screw-M3x018"
  Placement = pos=(-250.35,37.29,10) rot=(0.57735,0.57735,-0.57735;2.0944rad)
  shape: bbox 5.5 x 19 x 5.5 mm, 16 faces (baked)
FEATURE [Part::Feature] Chamfer016  label="ISO4762_Hex_screw-M3x019"
  Placement = pos=(-250.35,37.29,20) rot=(0.57735,0.57735,-0.57735;2.0944rad)
  shape: bbox 5.5 x 19 x 5.5 mm, 16 faces (baked)
FEATURE [Part::Feature] Compound001  label="Servo-Futaba-3003-ready002"
  Placement = pos=(-203,69.69,14.95) rot=(0,0.707107,-0.707107;3.14159rad)
  shape: bbox 57.75 x 41.74 x 20 mm, 378 faces, 4 solids (baked)
FEATURE [Part::Feature] Chamfer017  label="ISO4032-Hex-Nut-M007"
  Placement = pos=(-227.45,48.49,20) rot=(0,0,1;0rad)
  shape: bbox 6.35 x 2.4 x 6.35 mm, 29 faces (baked)
FEATURE [Part::Feature] Chamfer018  label="ISO4032-Hex-Nut-M008"
  Placement = pos=(-227.45,48.69,10) rot=(0,0,1;0rad)
  shape: bbox 6.35 x 2.4 x 6.35 mm, 29 faces (baked)
FEATURE [Part::Feature] Chamfer019  label="ISO4032-Hex-Nut-M009"
  Placement = pos=(-178.45,48.49,10) rot=(0,0,1;0rad)
  shape: bbox 6.35 x 2.4 x 6.35 mm, 29 faces (baked)
FEATURE [Part::Feature] Chamfer020  label="ISO4032-Hex-Nut-M010"
  Placement = pos=(-178.45,48.49,20) rot=(0,0,1;0rad)
  shape: bbox 6.35 x 2.4 x 6.35 mm, 29 faces (baked)
FEATURE [Part::Feature] Chamfer021  label="ISO4762_Hex_screw-M3x020"
  Placement = pos=(-227.45,37.49,20) rot=(0.57735,0.57735,-0.57735;2.0944rad)
  shape: bbox 5.5 x 19 x 5.5 mm, 16 faces (baked)
FEATURE [Part::Feature] Chamfer022  label="ISO4762_Hex_screw-M3x021"
  Placement = pos=(-178.45,37.49,10) rot=(0.57735,0.57735,-0.57735;2.0944rad)
  shape: bbox 5.5 x 19 x 5.5 mm, 16 faces (baked)
FEATURE [Part::Feature] Chamfer023  label="ISO4762_Hex_screw-M3x022"
  Placement = pos=(-178.45,37.49,20) rot=(0.57735,0.57735,-0.57735;2.0944rad)
  shape: bbox 5.5 x 19 x 5.5 mm, 16 faces (baked)
FEATURE [Part::Feature] Chamfer024  label="ISO4762_Hex_screw-M3x023"
  Placement = pos=(-227.45,37.49,10) rot=(0.57735,0.57735,-0.57735;2.0944rad)
  shape: bbox 5.5 x 19 x 5.5 mm, 16 faces (baked)
FEATURE [Part::Feature] Fillet018015  label="rounded-horn"
  Placement = pos=(-212.45,31.6,14.95) rot=(0.707107,0,-0.707107;3.14159rad)
  shape: bbox 21 x 6.2 x 21 mm, 65 faces (baked)
FEATURE [Part::Feature] Fillet018016  label="rounded-horn001"
  Placement = pos=(-212.45,52.9,64.75) rot=(-0.57735,0.57735,-0.57735;2.0944rad)
  shape: bbox 21 x 21 x 6.2 mm, 65 faces (baked)
FEATURE [Part::Feature] Fillet018017  label="horn-screw"
  Placement = pos=(-205,55.995,59.15) rot=(0,0.707107,-0.707107;3.14159rad)
  shape: bbox 4.8 x 4.8 x 5.5 mm, 21 faces (baked)
FEATURE [Part::Feature] Fillet018018  label="horn-screw001"
  Placement = pos=(-212.45,45.45,59.15) rot=(0,0.707107,-0.707107;3.14159rad)
  shape: bbox 4.8 x 4.8 x 5.5 mm, 21 faces (baked)
FEATURE [Part::Feature] Fillet018019  label="horn-screw002"
  Placement = pos=(-219.9,55.245,59.15) rot=(0,0.707107,-0.707107;3.14159rad)
  shape: bbox 4.8 x 4.8 x 5.5 mm, 21 faces (baked)
FEATURE [Part::Feature] Fillet018020  label="horn-screw003"
  Placement = pos=(-205,26,11.855) rot=(0.707107,0,0.707107;3.14159rad)
  shape: bbox 4.8 x 5.5 x 4.8 mm, 21 faces (baked)
FEATURE [Part::Feature] Fillet018021  label="horn-screw004"
  Placement = pos=(-212.45,26,22.4) rot=(0.707107,0,0.707107;3.14159rad)
  shape: bbox 4.8 x 5.5 x 4.8 mm, 21 faces (baked)
FEATURE [Part::Feature] Fillet018022  label="horn-screw005"
  Placement = pos=(-219.9,26,11.855) rot=(0.707107,0,0.707107;3.14159rad)
  shape: bbox 4.8 x 5.5 x 4.8 mm, 21 faces (baked)
FEATURE [Part::Feature] Fillet018023  label="rounded-horn002"
  Placement = pos=(-265.45,31.4,14.95) rot=(0.707107,0,-0.707107;3.14159rad)
  shape: bbox 21 x 6.2 x 21 mm, 65 faces (baked)
FEATURE [Part::Feature] Fillet018024  label="horn-screw006"
  Placement = pos=(-265.45,25.8,22.4) rot=(0.707107,0,0.707107;3.14159rad)
  shape: bbox 4.8 x 5.5 x 4.8 mm, 21 faces (baked)
FEATURE [Part::Feature] Fillet018025  label="horn-screw007"
  Placement = pos=(-258,25.8,11.855) rot=(0.707107,0,0.707107;3.14159rad)
  shape: bbox 4.8 x 5.5 x 4.8 mm, 21 faces (baked)
FEATURE [Part::Feature] Fillet018026  label="horn-screw008"
  Placement = pos=(-272.9,25.8,11.855) rot=(0.707107,0,0.707107;3.14159rad)
  shape: bbox 4.8 x 5.5 x 4.8 mm, 21 faces (baked)
FEATURE [Part::Feature] Fillet018027  label="rounded-horn003"
  Placement = pos=(-265.45,52.9,64.75) rot=(-0.57735,0.57735,-0.57735;2.0944rad)
  shape: bbox 21 x 21 x 6.2 mm, 65 faces (baked)
FEATURE [Part::Feature] Fillet018028  label="horn-screw009"
  Placement = pos=(-265.45,45.45,59.15) rot=(0,0.707107,-0.707107;3.14159rad)
  shape: bbox 4.8 x 4.8 x 5.5 mm, 21 faces (baked)
FEATURE [Part::Feature] Fillet018029  label="horn-screw010"
  Placement = pos=(-272.9,55.245,59.15) rot=(0,0.707107,-0.707107;3.14159rad)
  shape: bbox 4.8 x 4.8 x 5.5 mm, 21 faces (baked)
FEATURE [Part::Feature] Fillet018030  label="horn-screw011"
  Placement = pos=(-258,55.995,59.15) rot=(0,0.707107,-0.707107;3.14159rad)
  shape: bbox 4.8 x 4.8 x 5.5 mm, 21 faces (baked)
FEATURE [Part::Feature] Compound002  label="BQ-zum-BT-328"
  Placement = pos=(-275.3,70,2.24) rot=(0,0,-1;1.5708rad)
  shape: bbox 74.88 x 14.12 x 53.36 mm, 2412 faces, 7 solids (baked)
FEATURE [Part::Feature] Chamfer025  label="ISO4762_Hex_screw-M3x10"
  Placement = pos=(-246,80.8,113.94) rot=(0.57735,0.57735,-0.57735;2.0944rad)
  shape: bbox 5.5 x 13 x 5.5 mm, 16 faces (baked)
FEATURE [Part::Feature] Chamfer026  label="ISO4762_Hex_screw-M3x024"
  Placement = pos=(-226,80.8,113.94) rot=(0.57735,0.57735,-0.57735;2.0944rad)
  shape: bbox 5.5 x 13 x 5.5 mm, 16 faces (baked)
FEATURE [Part::Feature] Chamfer027  label="ISO4762_Hex_screw-M3x025"
  Placement = pos=(-246,80.8,93.94) rot=(0.57735,0.57735,-0.57735;2.0944rad)
  shape: bbox 5.5 x 13 x 5.5 mm, 16 faces (baked)
FEATURE [Part::Feature] Chamfer028  label="ISO4762_Hex_screw-M3x026"
  Placement = pos=(-226,80.8,93.94) rot=(0.57735,0.57735,-0.57735;2.0944rad)
  shape: bbox 5.5 x 13 x 5.5 mm, 16 faces (baked)
FEATURE [Part::Feature] Chamfer029  label="ISO4032-Hex-Nut-M011"
  Placement = pos=(-226,87.5,113.94) rot=(0,0,1;0rad)
  shape: bbox 6.35 x 2.4 x 6.35 mm, 29 faces (baked)
FEATURE [Part::Feature] Chamfer030  label="ISO4032-Hex-Nut-M012"
  Placement = pos=(-246,87.5,113.94) rot=(0,0,1;0rad)
  shape: bbox 6.35 x 2.4 x 6.35 mm, 29 faces (baked)
FEATURE [Part::Feature] Chamfer031  label="ISO4032-Hex-Nut-M013"
  Placement = pos=(-226,87.5,93.94) rot=(0,0,1;0rad)
  shape: bbox 6.35 x 2.4 x 6.35 mm, 29 faces (baked)
FEATURE [Part::Feature] Chamfer032  label="ISO4762_Hex_screw-M3x027"
  Placement = pos=(-246,80.8,93.94) rot=(0.57735,0.57735,-0.57735;2.0944rad)
  shape: bbox 5.5 x 13 x 5.5 mm, 16 faces (baked)
FEATURE [Part::Feature] Chamfer033  label="ISO4032-Hex-Nut-M014"
  Placement = pos=(-246,87.5,93.94) rot=(0,0,1;0rad)
  shape: bbox 6.35 x 2.4 x 6.35 mm, 29 faces (baked)
FEATURE [Part::Feature] Compound003  label="Servo-Futaba-3003-ready003"
  Placement = pos=(-265.45,43.45,102.84) rot=(0.707107,0.707107,0;3.14159rad)
  shape: bbox 20 x 57.75 x 41.74 mm, 378 faces, 4 solids (baked)
FEATURE [Part::Feature] Compound004  label="Servo-Futaba-3003-ready004"
  Placement = pos=(-212.45,43.45,102.84) rot=(0.707107,0.707107,0;3.14159rad)
  shape: bbox 20 x 57.75 x 41.74 mm, 378 faces, 4 solids (baked)
FEATURE [Part::Feature] Chamfer034  label="ISO4762_Hex_screw-M3x12"
  Placement = pos=(-270.5,19,68.54) rot=(0.707107,-0.707107,0;3.14159rad)
  shape: bbox 5.5 x 5.5 x 15 mm, 16 faces (baked)
FEATURE [Part::Feature] Chamfer035  label="ISO4762_Hex_screw-M3x028"
  Placement = pos=(-260.5,19,68.54) rot=(0.707107,-0.707107,0;3.14159rad)
  shape: bbox 5.5 x 5.5 x 15 mm, 16 faces (baked)
FEATURE [Part::Feature] Chamfer036  label="ISO4762_Hex_screw-M3x029"
  Placement = pos=(-260.5,68,68.54) rot=(0.707107,-0.707107,0;3.14159rad)
  shape: bbox 5.5 x 5.5 x 15 mm, 16 faces (baked)
FEATURE [Part::Feature] Chamfer037  label="ISO4762_Hex_screw-M3x030"
  Placement = pos=(-270.5,68,68.54) rot=(0.707107,-0.707107,0;3.14159rad)
  shape: bbox 5.5 x 5.5 x 15 mm, 16 faces (baked)
FEATURE [Part::Feature] Chamfer038  label="ISO4762_Hex_screw-M3x031"
  Placement = pos=(-217.5,68,68.54) rot=(0.707107,-0.707107,0;3.14159rad)
  shape: bbox 5.5 x 5.5 x 15 mm, 16 faces (baked)
FEATURE [Part::Feature] Chamfer039  label="ISO4762_Hex_screw-M3x032"
  Placement = pos=(-207.5,68,68.54) rot=(0.707107,-0.707107,0;3.14159rad)
  shape: bbox 5.5 x 5.5 x 15 mm, 16 faces (baked)
FEATURE [Part::Feature] Chamfer040  label="ISO4762_Hex_screw-M3x033"
  Placement = pos=(-217.5,19,68.54) rot=(0.707107,-0.707107,0;3.14159rad)
  shape: bbox 5.5 x 5.5 x 15 mm, 16 faces (baked)
FEATURE [Part::Feature] Chamfer041  label="ISO4762_Hex_screw-M3x034"
  Placement = pos=(-207.5,19,68.54) rot=(0.707107,-0.707107,0;3.14159rad)
  shape: bbox 5.5 x 5.5 x 15 mm, 16 faces (baked)
FEATURE [Part::Feature] Chamfer042  label="ISO4032-Hex-Nut-M015"
  Placement = pos=(-260.5,19,77.04) rot=(0.57735,-0.57735,-0.57735;2.0944rad)
  shape: bbox 6.35 x 6.35 x 2.4 mm, 29 faces (baked)
FEATURE [Part::Feature] Chamfer043  label="ISO4032-Hex-Nut-M016"
  Placement = pos=(-270.5,68,77.04) rot=(0.57735,-0.57735,-0.57735;2.0944rad)
  shape: bbox 6.35 x 6.35 x 2.4 mm, 29 faces (baked)
FEATURE [Part::Feature] Chamfer044  label="ISO4032-Hex-Nut-M017"
  Placement = pos=(-260.5,68,77.04) rot=(0.57735,-0.57735,-0.57735;2.0944rad)
  shape: bbox 6.35 x 6.35 x 2.4 mm, 29 faces (baked)
FEATURE [Part::Feature] Chamfer045  label="ISO4032-Hex-Nut-M018"
  Placement = pos=(-270.5,19,77.04) rot=(0.57735,-0.57735,-0.57735;2.0944rad)
  shape: bbox 6.35 x 6.35 x 2.4 mm, 29 faces (baked)
FEATURE [Part::Feature] Chamfer046  label="ISO4032-Hex-Nut-M019"
  Placement = pos=(-217.5,19,77.04) rot=(0.57735,-0.57735,-0.57735;2.0944rad)
  shape: bbox 6.35 x 6.35 x 2.4 mm, 29 faces (baked)
FEATURE [Part::Feature] Chamfer047  label="ISO4032-Hex-Nut-M020"
  Placement = pos=(-207.5,19,77.04) rot=(0.57735,-0.57735,-0.57735;2.0944rad)
  shape: bbox 6.35 x 6.35 x 2.4 mm, 29 faces (baked)
FEATURE [Part::Feature] Chamfer048  label="ISO4032-Hex-Nut-M021"
  Placement = pos=(-207.5,68,77.04) rot=(0.57735,-0.57735,-0.57735;2.0944rad)
  shape: bbox 6.35 x 6.35 x 2.4 mm, 29 faces (baked)
FEATURE [Part::Feature] Chamfer049  label="ISO4032-Hex-Nut-M022"
  Placement = pos=(-217.5,68,77.04) rot=(0.57735,-0.57735,-0.57735;2.0944rad)
  shape: bbox 6.35 x 6.35 x 2.4 mm, 29 faces (baked)
FEATURE [Part::Feature] Cut073  label="Shaft-bolt001"
  Placement = pos=(-265.402,52.9083,67.75) rot=(0.707107,-0.707107,0;3.14159rad)
  shape: bbox 5.38 x 5.38 x 9.391 mm, 18 faces (baked)
FEATURE [App::DocumentObjectGroup] Group011  label="Left-leg-group"
  Group = -> [Part__Mirroring007004,Fillet018027,Fillet018028,Fillet018029,Fillet018030,Fillet018023,Fillet018024,Fillet018025,Fillet018026,Cut073]
FEATURE [Part::Feature] Cut074  label="Shaft-bolt002"
  Placement = pos=(-212.402,52.9083,67.75) rot=(0.707107,-0.707107,0;3.14159rad)
  shape: bbox 5.38 x 5.38 x 9.391 mm, 18 faces (baked)
FEATURE [App::DocumentObjectGroup] Group012  label="Right-leg-group"
  Group = -> [Part__Mirroring007003,Fillet018015,Fillet018016,Fillet018017,Fillet018018,Fillet018019,Fillet018020,Fillet018021,Fillet018022,Cut074]
FEATURE [App::DocumentObjectGroup] Group010  label="Legs"
  Group = -> [Group011,Group012]
FEATURE [App::DocumentObjectGroup] Group014  label="Right-foot"
  Group = -> [Compound001,Part__Mirroring007002,Chamfer021,Chamfer024,Chamfer018,Chamfer017,Chamfer008,Chamfer023,Chamfer020,Chamfer019,Chamfer022]
FEATURE [App::DocumentObjectGroup] Group015  label="Left-foot"
  Group = -> [Chamfer007,Chamfer009,Chamfer010,Chamfer011,Chamfer012,Chamfer013,Compound,Chamfer014,Chamfer015,Chamfer016,Cut071]
FEATURE [App::DocumentObjectGroup] Group009  label="Feet"
  Group = -> [Group014,Group015]
FEATURE [Part::Feature] Part__Feature024  label="BAT-ultrasound"
  Placement = pos=(-238.5,86.68,61.94) rot=(0,0,-1;1.5708rad)
  shape: bbox 56 x 18.72 x 27.52 mm, 81 faces (baked)
FEATURE [Part::Feature] Chamfer050  label="ISO4032-Hex-Nut-M023"
  Placement = pos=(-272,78.5,73.94) rot=(0,0,-1;1.5708rad)
  shape: bbox 2.4 x 6.35 x 6.35 mm, 29 faces (baked)
FEATURE [Part::Feature] Chamfer051  label="ISO4032-Hex-Nut-M024"
  Placement = pos=(-208.2,78.5,73.94) rot=(0,0,-1;1.5708rad)
  shape: bbox 2.4 x 6.35 x 6.35 mm, 29 faces (baked)
FEATURE [Part::Compound] Compound005  label="batteries"
  Placement = pos=(-237.75,42.55,94.79) rot=(-0.57735,0.57735,-0.57735;2.0944rad)
FEATURE [Part::Compound] Compound006  label="battery-holder"
  Placement = pos=(-237.75,42.55,94.79) rot=(-0.57735,0.57735,-0.57735;2.0944rad)
FEATURE [App::DocumentObjectGroup] Group013  label="Body"
  Group = -> [Chamfer006,Chamfer025,Chamfer026,Chamfer027,Chamfer028,Chamfer029,Chamfer030,Chamfer031,Chamfer032,Chamfer033,Compound003,Compound004,Chamfer034,Chamfer035,Chamfer036,Chamfer037,Chamfer038,Chamfer039,Chamfer040,Chamfer041,Chamfer042,Chamfer043,Chamfer044,Chamfer045,Chamfer046,Chamfer047,Chamfer048,Chamfer049,Compound002,Chamfer050,Chamfer051,Compound005,Compound006]
FEATURE [Part::Feature] Chamfer052  label="ISO4762_Hex_screw-M3x035"
  Placement = pos=(-199.1,78.5,73.94) rot=(-0.57735,0.57735,-0.57735;2.0944rad)
  shape: bbox 13 x 5.5 x 5.5 mm, 16 faces (baked)
FEATURE [Part::Feature] Chamfer053  label="ISO4762_Hex_screw-M3x036"
  Placement = pos=(-278.9,78.5,73.94) rot=(0.57735,0.57735,-0.57735;4.18879rad)
  shape: bbox 13 x 5.5 x 5.5 mm, 16 faces (baked)
FEATURE [App::DocumentObjectGroup] Group016  label="Head"
  Group = -> [Cut072,Part__Feature024,Chamfer052,Chamfer053]
FEATURE [Part::Feature] Fusion043  label="soft-drink-can"
  Placement = pos=(-397.85,47.19,0) rot=(0,0,-1;1.5708rad)
  shape: bbox 66.1 x 66.1 x 115.2 mm, 53 faces (baked)
FEATURE [App::DocumentObjectGroup] Group018  label="development"
  Group = -> [Group006,Group002]
FEATURE [Part::Feature] Cut075  label="pie-D002"
  Placement = pos=(-91.85,121.19,3) rot=(0,0,-1;1.5708rad)
  shape: bbox 58 x 72 x 24 mm, 84 faces (baked)
FEATURE [Part::Feature] Chamfer054  label="body"
  Placement = pos=(-36,25,-63) rot=(0,0,-1;1.5708rad)
  shape: bbox 80 x 80 x 55 mm, 159 faces (baked)
FEATURE [Part::Feature] Cut076  label="head002"
  Placement = pos=(-36,83.4171,131) rot=(0.707107,0.707107,0;3.14159rad)
  shape: bbox 80 x 80 x 63 mm, 68 faces (baked)
FEATURE [Part::Feature] Part__Mirroring007005  label="leg-body001"
  Placement = pos=(-126.49,24.7,1.00001) rot=(-0.57735,0.57735,-0.57735;2.0944rad)
  shape: bbox 59.5 x 53 x 21 mm, 32 faces (baked)
FEATURE [Part::Feature] Chamfer055  label="ISO-10642-M3x012"
  Placement = pos=(292,105.8,0) rot=(0.57735,-0.57735,-0.57735;4.18879rad)
  shape: bbox 6.046 x 10 x 6.046 mm, 25 faces (baked)
FEATURE [Part::Feature] Chamfer056  label="ISO4762_Hex_screw-M3x037"
  Placement = pos=(175.261,55.2049,0) rot=(0.57735,-0.57735,-0.57735;4.18879rad)
  shape: bbox 5.5 x 19 x 5.5 mm, 16 faces (baked)
FEATURE [Part::Feature] Fillet018031  label="rounded-horn004"
  Placement = pos=(194.771,-98.3346,-3.5) rot=(0,0.707107,0.707107;3.14159rad)
  shape: bbox 21 x 21 x 6.2 mm, 65 faces (baked)
FEATURE [Part::Feature] Fillet018032  label="horn-screw012"
  Placement = pos=(186.541,-124.135,-4.7e-11) rot=(1,0,0;3.14159rad)
  shape: bbox 4.8 x 5.5 x 4.8 mm, 21 faces (baked)
FEATURE [Part::Feature] Compound007  label="BQ-zum-BT-329"
  Placement = pos=(367.657,-106.612,10.8) rot=(0.57735,0.57735,0.57735;4.18879rad)
  shape: bbox 74.88 x 53.36 x 14.12 mm, 2412 faces, 7 solids (baked)
FEATURE [Part::Feature] Compound008  label="Servo-Futaba-3003-ready005"
  Placement = pos=(195.374,-44.1703,-0.6) rot=(0,0,-1;1.5708rad)
  shape: bbox 20 x 57.75 x 41.74 mm, 378 faces, 4 solids (baked)
FEATURE [Part::Feature] Cut077  label="Shaft-bolt003"
  Placement = pos=(207.465,-116.835,0) rot=(1,0,0;1.5708rad)
  shape: bbox 5.38 x 9.391 x 5.38 mm, 18 faces (baked)
FEATURE [Part::Feature] Part__Feature025  label="BAT-ultrasound001"
  Placement = pos=(485.708,-48.0945,-70) rot=(0.57735,0.57735,0.57735;4.18879rad)
  shape: bbox 56 x 27.52 x 18.72 mm, 81 faces (baked)
FEATURE [App::Annotation] Text
  LabelText = Bolts / Tornillos
  Position = (168.645,133.318,0)
FEATURE [App::Annotation] Text001
  LabelText = ISO 4762 | M3x10
  Position = (265.965,64.8263,0)
FEATURE [Part::Feature] Chamfer057  label="ISO4762_Hex_screw-M3x038"
  Placement = pos=(267.828,50.8969,0) rot=(-1,0,0;1.5708rad)
  shape: bbox 5.5 x 13 x 5.5 mm, 16 faces (baked)
FEATURE [Part::Feature] Chamfer058  label="ISO4762_Hex_screw-M3x039"
  Placement = pos=(279.523,50.8969,0) rot=(-1,0,0;1.5708rad)
  shape: bbox 5.5 x 13 x 5.5 mm, 16 faces (baked)
FEATURE [Part::Part2DObjectPython] Rectangle  # Draft 2D object (typed FeaturePython)
  ChamferSize = 0
  FilletRadius = 3
  Height = -17.0597
  Length = 24.2627
  MakeFace = false
  Placement = pos=(261.55,55.9879,0) rot=(0,0,1;0rad)
FEATURE [App::Annotation] Text002
  LabelText = Head
  Position = (267.362,33.3223,0)
FEATURE [App::Annotation] Text003
  LabelText = Electronics / Electronica
  Position = (369.29,55.2609,0)
FEATURE [App::Annotation] Text004
  LabelText = Ultrasound BAT
  Position = (457.399,37.0732,0)
FEATURE [App::Annotation] Text005
  LabelText = BQ ZUM BT-328
  Position = (371.01,36.6659,0)
FEATURE [Part::Feature] Chamfer059  label="ISO4762_Hex_screw-M3x040"
  Placement = pos=(298.78,50.8969,0) rot=(-1,0,0;1.5708rad)
  shape: bbox 5.5 x 13 x 5.5 mm, 16 faces (baked)
FEATURE [Part::Feature] Chamfer060  label="ISO4762_Hex_screw-M3x041"
  Placement = pos=(308.523,50.8969,0) rot=(-1,0,0;1.5708rad)
  shape: bbox 5.5 x 13 x 5.5 mm, 16 faces (baked)
FEATURE [Part::Feature] Chamfer061  label="ISO4762_Hex_screw-M3x042"
  Placement = pos=(318.523,50.8969,0) rot=(-1,0,0;1.5708rad)
  shape: bbox 5.5 x 13 x 5.5 mm, 16 faces (baked)
FEATURE [Part::Feature] Chamfer062  label="ISO4762_Hex_screw-M3x043"
  Placement = pos=(328.523,50.8969,0) rot=(-1,0,0;1.5708rad)
  shape: bbox 5.5 x 13 x 5.5 mm, 16 faces (baked)
FEATURE [App::Annotation] Text006
  LabelText = BQ ZUM
  Position = (306.362,33.3223,0)
FEATURE [Part::Part2DObjectPython] Rectangle001  # Draft 2D object (typed FeaturePython)
  ChamferSize = 0
  FilletRadius = 3
  Height = -19
  Length = 43
  MakeFace = false
  Placement = pos=(292.261,57.1049,0) rot=(0,0,1;0rad)
FEATURE [App::Annotation] Text007
  LabelText = Nuts / Tuercas
  Position = (368.32,138.38,0)
FEATURE [App::Annotation] Text008
  LabelText = ISO 4032 | M3
  Position = (358.837,123.601,0)
FEATURE [Part::Feature] Chamfer063  label="ISO4032-Hex-Nut-M025"
  Placement = pos=(367.861,111.46,0) rot=(1,0,0;1.5708rad)
  shape: bbox 6.35 x 6.35 x 2.4 mm, 29 faces (baked)
FEATURE [Part::Feature] Chamfer064  label="ISO4032-Hex-Nut-M026"
  Placement = pos=(375.782,111.46,0) rot=(1,0,0;1.5708rad)
  shape: bbox 6.35 x 6.35 x 2.4 mm, 29 faces (baked)
FEATURE [Part::Feature] Chamfer065  label="ISO4032-Hex-Nut-M027"
  Placement = pos=(383.457,111.46,0) rot=(1,0,0;1.5708rad)
  shape: bbox 6.35 x 6.35 x 2.4 mm, 29 faces (baked)
FEATURE [Part::Feature] Chamfer066  label="ISO4032-Hex-Nut-M028"
  Placement = pos=(391.457,111.46,0) rot=(1,0,0;1.5708rad)
  shape: bbox 6.35 x 6.35 x 2.4 mm, 29 faces (baked)
FEATURE [Part::Feature] Chamfer067  label="ISO4032-Hex-Nut-M029"
  Placement = pos=(399.303,111.46,0) rot=(1,0,0;1.5708rad)
  shape: bbox 6.35 x 6.35 x 2.4 mm, 29 faces (baked)
FEATURE [Part::Feature] Chamfer068  label="ISO4032-Hex-Nut-M030"
  Placement = pos=(407.303,111.46,0) rot=(1,0,0;1.5708rad)
  shape: bbox 6.35 x 6.35 x 2.4 mm, 29 faces (baked)
FEATURE [Part::Feature] Compound011  label="Batteries-8xAAA"
  Placement = pos=(431.766,-86.5105,0) rot=(0,-1,0;1.5708rad)
  shape: bbox 61.16 x 52.32 x 31.6 mm, 1281 faces, 61 solids (baked)
FEATURE [App::Annotation] Text009
  LabelText = 8-AAA batteries | Battery holder
  Position = (371.448,-50.1574,0)
FEATURE [App::Annotation] Text010
  LabelText = Futaba 3003 Servos
  Position = (206.931,-1.39589,0)
FEATURE [Part::Feature] Compound012  label="Servo-Futaba-3003-ready006"
  Placement = pos=(233.374,-44.1703,-0.6) rot=(0,0,-1;1.5708rad)
  shape: bbox 20 x 57.75 x 41.74 mm, 378 faces, 4 solids (baked)
FEATURE [Part::Feature] Compound013  label="Servo-Futaba-3003-ready007"
  Placement = pos=(271.374,-44.1703,-0.6) rot=(0,0,-1;1.5708rad)
  shape: bbox 20 x 57.75 x 41.74 mm, 378 faces, 4 solids (baked)
FEATURE [Part::Feature] Compound014  label="Servo-Futaba-3003-ready008"
  Placement = pos=(311.374,-44.1703,-0.6) rot=(0,0,-1;1.5708rad)
  shape: bbox 20 x 57.75 x 41.74 mm, 378 faces, 4 solids (baked)
FEATURE [Part::Feature] Chamfer069  label="ISO4762_Hex_screw-M3x044"
  Placement = pos=(176.261,105.105,0) rot=(-1,0,0;1.5708rad)
  shape: bbox 5.5 x 15 x 5.5 mm, 16 faces (baked)
FEATURE [App::Annotation] Text011
  LabelText = ISO 4762 | M3x12
  Position = (169.261,120.105,0)
FEATURE [Part::Feature] Chamfer070  label="ISO4762_Hex_screw-M3x045"
  Placement = pos=(188.261,105.105,0) rot=(-1,0,0;1.5708rad)
  shape: bbox 5.5 x 15 x 5.5 mm, 16 faces (baked)
FEATURE [Part::Feature] Chamfer071  label="ISO4762_Hex_screw-M3x046"
  Placement = pos=(200.261,105.105,0) rot=(-1,0,0;1.5708rad)
  shape: bbox 5.5 x 15 x 5.5 mm, 16 faces (baked)
FEATURE [Part::Feature] Chamfer072  label="ISO4762_Hex_screw-M3x047"
  Placement = pos=(212.261,105.105,0) rot=(-1,0,0;1.5708rad)
  shape: bbox 5.5 x 15 x 5.5 mm, 16 faces (baked)
FEATURE [Part::Feature] Chamfer073  label="ISO4762_Hex_screw-M3x048"
  Placement = pos=(259.261,105.105,0) rot=(-1,0,0;1.5708rad)
  shape: bbox 5.5 x 15 x 5.5 mm, 16 faces (baked)
FEATURE [Part::Feature] Chamfer074  label="ISO4762_Hex_screw-M3x049"
  Placement = pos=(247.261,105.105,0) rot=(-1,0,0;1.5708rad)
  shape: bbox 5.5 x 15 x 5.5 mm, 16 faces (baked)
FEATURE [Part::Feature] Chamfer075  label="ISO4762_Hex_screw-M3x050"
  Placement = pos=(235.261,105.105,0) rot=(-1,0,0;1.5708rad)
  shape: bbox 5.5 x 15 x 5.5 mm, 16 faces (baked)
FEATURE [Part::Feature] Chamfer076  label="ISO4762_Hex_screw-M3x051"
  Placement = pos=(223.261,105.105,0) rot=(-1,0,0;1.5708rad)
  shape: bbox 5.5 x 15 x 5.5 mm, 16 faces (baked)
FEATURE [Part::Feature] Chamfer077  label="ISO4032-Hex-Nut-M031"
  Placement = pos=(368.191,101.058,2.01531) rot=(1,0,0;1.5708rad)
  shape: bbox 6.35 x 6.35 x 2.4 mm, 29 faces (baked)
FEATURE [Part::Feature] Chamfer078  label="ISO4032-Hex-Nut-M032"
  Placement = pos=(375.787,101.058,2.01531) rot=(1,0,0;1.5708rad)
  shape: bbox 6.35 x 6.35 x 2.4 mm, 29 faces (baked)
FEATURE [Part::Feature] Chamfer079  label="ISO4032-Hex-Nut-M033"
  Placement = pos=(383.275,101.058,2.01531) rot=(1,0,0;1.5708rad)
  shape: bbox 6.35 x 6.35 x 2.4 mm, 29 faces (baked)
FEATURE [Part::Feature] Chamfer080  label="ISO4032-Hex-Nut-M034"
  Placement = pos=(391.275,101.058,2.01531) rot=(1,0,0;1.5708rad)
  shape: bbox 6.35 x 6.35 x 2.4 mm, 29 faces (baked)
FEATURE [Part::Feature] Chamfer081  label="ISO4032-Hex-Nut-M035"
  Placement = pos=(422.275,101.058,2.01531) rot=(1,0,0;1.5708rad)
  shape: bbox 6.35 x 6.35 x 2.4 mm, 29 faces (baked)
FEATURE [Part::Feature] Chamfer082  label="ISO4032-Hex-Nut-M036"
  Placement = pos=(399.191,101.058,2.01531) rot=(1,0,0;1.5708rad)
  shape: bbox 6.35 x 6.35 x 2.4 mm, 29 faces (baked)
FEATURE [Part::Feature] Chamfer083  label="ISO4032-Hex-Nut-M037"
  Placement = pos=(406.787,101.058,2.01531) rot=(1,0,0;1.5708rad)
  shape: bbox 6.35 x 6.35 x 2.4 mm, 29 faces (baked)
FEATURE [Part::Feature] Chamfer084  label="ISO4032-Hex-Nut-M038"
  Placement = pos=(414.275,101.058,2.01531) rot=(1,0,0;1.5708rad)
  shape: bbox 6.35 x 6.35 x 2.4 mm, 29 faces (baked)
FEATURE [Part::Feature] Fillet018033  label="horn-screw013"
  Placement = pos=(193.541,-124.135,-4.7e-11) rot=(1,0,0;3.14159rad)
  shape: bbox 4.8 x 5.5 x 4.8 mm, 21 faces (baked)
FEATURE [Part::Feature] Fillet018034  label="rounded-horn005"
  Placement = pos=(232.771,-98.3346,-3.5) rot=(0,0.707107,0.707107;3.14159rad)
  shape: bbox 21 x 21 x 6.2 mm, 65 faces (baked)
FEATURE [Part::Feature] Cut078  label="Shaft-bolt004"
  Placement = pos=(245.465,-116.835,0) rot=(1,0,0;1.5708rad)
  shape: bbox 5.38 x 9.391 x 5.38 mm, 18 faces (baked)
FEATURE [Part::Feature] Fillet018035  label="horn-screw014"
  Placement = pos=(238.441,-124.135,-4.7e-11) rot=(1,0,0;3.14159rad)
  shape: bbox 4.8 x 5.5 x 4.8 mm, 21 faces (baked)
FEATURE [Part::Feature] Fillet018036  label="horn-screw015"
  Placement = pos=(224.541,-124.135,-4.7e-11) rot=(1,0,0;3.14159rad)
  shape: bbox 4.8 x 5.5 x 4.8 mm, 21 faces (baked)
FEATURE [Part::Feature] Fillet018037  label="horn-screw016"
  Placement = pos=(231.541,-124.135,-4.7e-11) rot=(1,0,0;3.14159rad)
  shape: bbox 4.8 x 5.5 x 4.8 mm, 21 faces (baked)
FEATURE [Part::Feature] Fillet018038  label="rounded-horn006"
  Placement = pos=(271.771,-98.3346,-3.5) rot=(0,0.707107,0.707107;3.14159rad)
  shape: bbox 21 x 21 x 6.2 mm, 65 faces (baked)
FEATURE [Part::Feature] Fillet018039  label="horn-screw017"
  Placement = pos=(263.541,-124.135,-4.7e-11) rot=(1,0,0;3.14159rad)
  shape: bbox 4.8 x 5.5 x 4.8 mm, 21 faces (baked)
FEATURE [Part::Feature] Cut079  label="Shaft-bolt005"
  Placement = pos=(284.465,-116.835,0) rot=(1,0,0;1.5708rad)
  shape: bbox 5.38 x 9.391 x 5.38 mm, 18 faces (baked)
FEATURE [Part::Feature] Fillet018040  label="horn-screw018"
  Placement = pos=(270.541,-124.135,-4.7e-11) rot=(1,0,0;3.14159rad)
  shape: bbox 4.8 x 5.5 x 4.8 mm, 21 faces (baked)
FEATURE [Part::Feature] Fillet018041  label="rounded-horn008"
  Placement = pos=(312.771,-98.3346,-3.5) rot=(0,0.707107,0.707107;3.14159rad)
  shape: bbox 21 x 21 x 6.2 mm, 65 faces (baked)
FEATURE [Part::Feature] Fillet018042  label="horn-screw023"
  Placement = pos=(304.541,-124.135,-4.7e-11) rot=(1,0,0;3.14159rad)
  shape: bbox 4.8 x 5.5 x 4.8 mm, 21 faces (baked)
FEATURE [Part::Feature] Cut080  label="Shaft-bolt006"
  Placement = pos=(325.465,-116.835,0) rot=(1,0,0;1.5708rad)
  shape: bbox 5.38 x 9.391 x 5.38 mm, 18 faces (baked)
FEATURE [Part::Feature] Fillet018043  label="horn-screw024"
  Placement = pos=(311.541,-124.135,-4.7e-11) rot=(1,0,0;3.14159rad)
  shape: bbox 4.8 x 5.5 x 4.8 mm, 21 faces (baked)
FEATURE [Part::Feature] Fillet018044  label="horn-screw025"
  Placement = pos=(318.441,-124.135,-4.7e-11) rot=(1,0,0;3.14159rad)
  shape: bbox 4.8 x 5.5 x 4.8 mm, 21 faces (baked)
FEATURE [Part::Feature] Fillet018045  label="horn-screw019"
  Placement = pos=(277.441,-124.135,-4.7e-11) rot=(1,0,0;3.14159rad)
  shape: bbox 4.8 x 5.5 x 4.8 mm, 21 faces (baked)
FEATURE [Part::Feature] Fillet018046  label="horn-screw026"
  Placement = pos=(200.441,-124.135,-4.7e-11) rot=(1,0,0;3.14159rad)
  shape: bbox 4.8 x 5.5 x 4.8 mm, 21 faces (baked)
FEATURE [Part::Part2DObjectPython] Rectangle002  # Draft 2D object (typed FeaturePython)
  ChamferSize = 0
  FilletRadius = 3
  Height = -20
  Length = 102
  MakeFace = false
  Placement = pos=(168.261,110.105,0) rot=(0,0,1;0rad)
FEATURE [App::Annotation] Text012
  LabelText = For attaching the servos to the body
  Position = (171.362,83.3223,0)
FEATURE [App::Annotation] Text013
  LabelText = ISO 4762 | M3x16
  Position = (170.261,70.1049,0)
FEATURE [Part::Feature] Chamfer085  label="ISO4762_Hex_screw-M3x052"
  Placement = pos=(184.261,55.2049,0) rot=(0.57735,-0.57735,-0.57735;4.18879rad)
  shape: bbox 5.5 x 19 x 5.5 mm, 16 faces (baked)
FEATURE [Part::Feature] Chamfer086  label="ISO4762_Hex_screw-M3x053"
  Placement = pos=(203.261,55.2049,0) rot=(0.57735,-0.57735,-0.57735;4.18879rad)
  shape: bbox 5.5 x 19 x 5.5 mm, 16 faces (baked)
FEATURE [Part::Feature] Chamfer087  label="ISO4762_Hex_screw-M3x054"
  Placement = pos=(194.261,55.2049,0) rot=(0.57735,-0.57735,-0.57735;4.18879rad)
  shape: bbox 5.5 x 19 x 5.5 mm, 16 faces (baked)
FEATURE [Part::Feature] Chamfer088  label="ISO4762_Hex_screw-M3x055"
  Placement = pos=(212.261,55.2049,0) rot=(0.57735,-0.57735,-0.57735;4.18879rad)
  shape: bbox 5.5 x 19 x 5.5 mm, 16 faces (baked)
FEATURE [Part::Feature] Chamfer089  label="ISO4762_Hex_screw-M3x056"
  Placement = pos=(221.261,55.2049,0) rot=(0.57735,-0.57735,-0.57735;4.18879rad)
  shape: bbox 5.5 x 19 x 5.5 mm, 16 faces (baked)
FEATURE [Part::Feature] Chamfer090  label="ISO4762_Hex_screw-M3x057"
  Placement = pos=(240.261,55.2049,0) rot=(0.57735,-0.57735,-0.57735;4.18879rad)
  shape: bbox 5.5 x 19 x 5.5 mm, 16 faces (baked)
FEATURE [Part::Feature] Chamfer091  label="ISO4762_Hex_screw-M3x058"
  Placement = pos=(231.261,55.2049,0) rot=(0.57735,-0.57735,-0.57735;4.18879rad)
  shape: bbox 5.5 x 19 x 5.5 mm, 16 faces (baked)
FEATURE [Part::Part2DObjectPython] Rectangle003  # Draft 2D object (typed FeaturePython)
  ChamferSize = 0
  FilletRadius = 3
  Height = -25
  Length = 79
  MakeFace = false
  Placement = pos=(170.261,61.1049,0) rot=(0,0,1;0rad)
FEATURE [App::Annotation] Text014
  LabelText = For attaching the servos to the feet
  Position = (171.362,30.3223,0)
FEATURE [Part::Feature] Chamfer092  label="ISO4032-Hex-Nut-M039"
  Placement = pos=(368.191,91.0583,2.01531) rot=(1,0,0;1.5708rad)
  shape: bbox 6.35 x 6.35 x 2.4 mm, 29 faces (baked)
FEATURE [Part::Feature] Chamfer093  label="ISO4032-Hex-Nut-M040"
  Placement = pos=(375.787,91.0583,2.01531) rot=(1,0,0;1.5708rad)
  shape: bbox 6.35 x 6.35 x 2.4 mm, 29 faces (baked)
FEATURE [Part::Feature] Chamfer094  label="ISO4032-Hex-Nut-M041"
  Placement = pos=(383.275,91.0583,2.01531) rot=(1,0,0;1.5708rad)
  shape: bbox 6.35 x 6.35 x 2.4 mm, 29 faces (baked)
FEATURE [Part::Feature] Chamfer095  label="ISO4032-Hex-Nut-M042"
  Placement = pos=(391.275,91.0583,2.01531) rot=(1,0,0;1.5708rad)
  shape: bbox 6.35 x 6.35 x 2.4 mm, 29 faces (baked)
FEATURE [Part::Feature] Chamfer096  label="ISO4032-Hex-Nut-M043"
  Placement = pos=(422.275,91.0583,2.01531) rot=(1,0,0;1.5708rad)
  shape: bbox 6.35 x 6.35 x 2.4 mm, 29 faces (baked)
FEATURE [Part::Feature] Chamfer097  label="ISO4032-Hex-Nut-M044"
  Placement = pos=(399.191,91.0583,2.01531) rot=(1,0,0;1.5708rad)
  shape: bbox 6.35 x 6.35 x 2.4 mm, 29 faces (baked)
FEATURE [Part::Feature] Chamfer098  label="ISO4032-Hex-Nut-M045"
  Placement = pos=(406.787,91.0583,2.01531) rot=(1,0,0;1.5708rad)
  shape: bbox 6.35 x 6.35 x 2.4 mm, 29 faces (baked)
FEATURE [Part::Feature] Chamfer099  label="ISO4032-Hex-Nut-M046"
  Placement = pos=(414.275,91.0583,2.01531) rot=(1,0,0;1.5708rad)
  shape: bbox 6.35 x 6.35 x 2.4 mm, 29 faces (baked)
FEATURE [Part::Feature] Chamfer100  label="ISO-10642-M3x013"
  Placement = pos=(301.566,105.8,0) rot=(0.57735,-0.57735,-0.57735;4.18879rad)
  shape: bbox 6.046 x 10 x 6.046 mm, 25 faces (baked)
FEATURE [App::Annotation] Text015
  LabelText = ISO 10642 | M3x10
  Position = (285.081,119.196,0)
FEATURE [Part::Part2DObjectPython] Rectangle004  # Draft 2D object (typed FeaturePython)
  ChamferSize = 0
  FilletRadius = 3
  Height = -20.1839
  Length = 31.1933
  MakeFace = false
  Placement = pos=(282.456,110.585,0) rot=(0,0,1;0rad)
FEATURE [App::Annotation] Text016
  LabelText = Feet Passive shaft
  Position = (281.259,83.8449,0)
FEATURE [Part::Part2DObjectPython] Rectangle005  # Draft 2D object (typed FeaturePython)
  ChamferSize = 5
  FilletRadius = 0
  Height = -130.677
  Length = 188.302
  MakeFace = false
  Placement = pos=(155.307,151.755,0) rot=(0,0,1;0rad)
FEATURE [App::DocumentObjectGroup] Group021  label="bolts"
  Group = -> [Text,Text001,Chamfer057,Chamfer058,Rectangle,Text002,Chamfer059,Chamfer060,Chamfer061,Chamfer062,Text006,Rectangle001,Chamfer069,Text011,Chamfer070,Chamfer071,Chamfer073,Chamfer072,Chamfer074,Chamfer075,Chamfer076,Rectangle002,Text012,Text013,Chamfer085,Chamfer086,Chamfer087,Chamfer088,Chamfer089,Chamfer090,Chamfer091,Rectangle003,Text014,Chamfer100,Chamfer055,Text015,Rectangle004,Text016,+2 more]
FEATURE [Part::Part2DObjectPython] Rectangle006  # Draft 2D object (typed FeaturePython)
  ChamferSize = 5
  FilletRadius = 0
  Height = -150.825
  Length = 189.46
  MakeFace = false
  Placement = pos=(155.802,15.421,0) rot=(0,0,1;0rad)
FEATURE [App::DocumentObjectGroup] Group024  label="Futaba-3003-servos"
  Group = -> [Text010,Compound012,Compound013,Compound014,Compound008,Fillet018033,Fillet018034,Cut078,Fillet018035,Fillet018036,Fillet018037,Fillet018038,Fillet018039,Cut079,Fillet018040,Fillet018041,Fillet018042,Cut080,Fillet018043,Fillet018044,Fillet018045,Fillet018046,Rectangle006,Fillet018031,Fillet018032,Cut077]
FEATURE [Part::Part2DObjectPython] Rectangle007  # Draft 2D object (typed FeaturePython)
  ChamferSize = 5
  FilletRadius = 0
  Height = -71.6908
  Length = 119.333
  MakeFace = false
  Placement = pos=(350.652,151.984,0) rot=(0,0,1;0rad)
FEATURE [App::DocumentObjectGroup] Group023  label="Nuts"
  Group = -> [Chamfer063,Chamfer064,Chamfer065,Chamfer066,Chamfer067,Chamfer068,Text007,Text008,Chamfer077,Chamfer078,Chamfer079,Chamfer080,Chamfer081,Chamfer082,Chamfer083,Chamfer084,Chamfer092,Chamfer093,Chamfer095,Chamfer094,Chamfer096,Chamfer097,Chamfer098,Chamfer099,Rectangle007]
FEATURE [Part::Part2DObjectPython] Rectangle008  # Draft 2D object (typed FeaturePython)
  ChamferSize = 5
  FilletRadius = 0
  Height = -199.251
  Length = 183.542
  MakeFace = false
  Placement = pos=(351.777,69.4013,0) rot=(0,0,1;0rad)
FEATURE [App::DocumentObjectGroup] Group022  label="Electronics"
  Group = -> [Text003,Text004,Part__Feature025,Text005,Compound007,Compound011,Text009,Rectangle008]
FEATURE [Part::Feature] Part__Mirroring007006  label="pie-I002"
  Placement = pos=(93.2202,119.745,2) rot=(0,0,-1;1.5708rad)
  shape: bbox 58 x 72 x 24 mm, 84 faces (baked)
FEATURE [Part::Feature] Part__Mirroring007007  label="pata-I002"
  Placement = pos=(129.293,25.8639,21.0392) rot=(0.57735,-0.57735,-0.57735;2.0944rad)
  shape: bbox 59.5 x 53 x 21 mm, 32 faces (baked)
FEATURE [App::Annotation] Text017
  LabelText = BOM: Bill of materials
  Position = (186.38,167.124,0)
FEATURE [App::DocumentObjectGroup] Group020  label="BOM"
  Group = -> [Group021,Group022,Group023,Group024,Text017]
FEATURE [Part::Part2DObjectPython] Rectangle009  # Draft 2D object (typed FeaturePython)
  ChamferSize = 5
  FilletRadius = 0
  Height = -207
  Length = 278
  MakeFace = false
  Placement = pos=(-137,151,0) rot=(0,0,1;0rad)
FEATURE [App::Annotation] Text018
  LabelText = Printed parts
  Position = (-49.6201,-83.8759,0)
FEATURE [App::DocumentObjectGroup] Group025  label="printed-parts"
  Group = -> [Chamfer054,Cut076,Part__Mirroring007006,Part__Mirroring007007,Cut075,Part__Mirroring007005,Rectangle009,Text018]
FEATURE [Part::Part2DObjectPython] Rectangle010  # Draft 2D object (typed FeaturePython)
  ChamferSize = 0
  FilletRadius = 0
  Height = -207
  Length = 301
  MakeFace = false
  Placement = pos=(-451,151,0) rot=(0,0,1;0rad)
FEATURE [App::Annotation] Text019
  LabelText = Assembly
  Position = (-319.62,-80.8759,0)
FEATURE [App::DocumentObjectGroup] Group017  label="Assembly"
  Group = -> [Group009,Group010,Group013,Group016,Fusion043,Rectangle010,Text019]
FEATURE [Part::Fillet] Fillet018013
  Base = -> Cut068
  Edges = 4 edges r=3: [Edge81,Edge84,Edge231,Edge247]
FEATURE [Part::Feature] Fillet018013001  label="Fillet018015"
  shape: bbox 80 x 80 x 55 mm, 127 faces (baked)
FEATURE [Part::Chamfer] Chamfer101
  Base = -> Fillet018013001
  Edges = 5 edges: [Edge1 r=4,Edge3 r=4,Edge5 r=4,Edge7 r=2.4,Edge13 r=2.4]
FEATURE [Part::Chamfer] Chamfer102
  Base = -> Chamfer101
  Edges = 3 edges: [Edge98 r=18,Edge124 r=1,Edge147 r=18]
FEATURE [Part::Box] Box048  label="Cube047"
  Height = 63
  Length = 80
  Placement = pos=(-23,-4,68) rot=(0,0,1;0rad)
  Width = 80
FEATURE [Part::Chamfer] Chamfer103
  Base = -> Box048
  Edges = 3 edges r=4: [Edge1,Edge2,Edge3]
FEATURE [Part::Cut] Cut081
  Base = -> Chamfer103
  Tool = -> Fillet006
FEATURE [Part::MultiFuse] Fusion044
  Shapes = -> [Fillet018014,Box020,Cylinder026,Cylinder016,Cylinder015,Cylinder014]
FEATURE [Part::Cut] Cut082
  Base = -> Cut081
  Tool = -> Fusion044
FEATURE [Part::FeaturePython] Clone004  label="Clone of Cut080026090"  # WARN: FeaturePython — macro-defined, semantics opaque (R4)
  Placement = pos=(20.8,4,-65) rot=(0,0,-1;1.5708rad)
  Scale = (1,1,1)
FEATURE [Part::FeaturePython] Clone006  label="Clone of Pad056"  # WARN: FeaturePython — macro-defined, semantics opaque (R4)
  Placement = pos=(-13.2,4,-69) rot=(0.57735,-0.57735,-0.57735;2.0944rad)
  Scale = (1,1,1)
FEATURE [Sketcher::SketchObject] Sketch009
  Placement = pos=(-40,0,0) rot=(0.57735,-0.57735,-0.57735;2.0944rad)
  sketch-geometry (19):
    g0: LineSegment StartX=-66 StartY=121.75 StartZ=0 EndX=-6 EndY=121.75 EndZ=0
    g1: LineSegment StartX=-6 StartY=121.75 StartZ=0 EndX=-6 EndY=117.5 EndZ=0
    g2: LineSegment StartX=-6 StartY=117.5 StartZ=0 EndX=-66 EndY=117.5 EndZ=0
    g3: LineSegment StartX=-66 StartY=117.5 StartZ=0 EndX=-66 EndY=121.75 EndZ=0
    g4: LineSegment StartX=-66 StartY=113.25 StartZ=0 EndX=-6 EndY=113.25 EndZ=0
    g5: LineSegment StartX=-6 StartY=113.25 StartZ=0 EndX=-6 EndY=109 EndZ=0
    g6: LineSegment StartX=-6 StartY=109 StartZ=0 EndX=-66 EndY=109 EndZ=0
    g7: LineSegment StartX=-66 StartY=109 StartZ=0 EndX=-66 EndY=113.25 EndZ=0
    g8: LineSegment StartX=-66 StartY=104.75 StartZ=0 EndX=-6 EndY=104.75 EndZ=0
    g9: LineSegment StartX=-6 StartY=104.75 StartZ=0 EndX=-6 EndY=100.5 EndZ=0
    g10: LineSegment StartX=-6 StartY=100.5 StartZ=0 EndX=-66 EndY=100.5 EndZ=0
    g11: LineSegment StartX=-66 StartY=100.5 StartZ=0 EndX=-66 EndY=104.75 EndZ=0
    g12: LineSegment StartX=-66 StartY=96.25 StartZ=0 EndX=-6 EndY=96.25 EndZ=0
    g13: LineSegment StartX=-6 StartY=96.25 StartZ=0 EndX=-6 EndY=92 EndZ=0
    g14: LineSegment StartX=-6 StartY=92 StartZ=0 EndX=-66 EndY=92 EndZ=0
    g15: LineSegment StartX=-66 StartY=92 StartZ=0 EndX=-66 EndY=96.25 EndZ=0
    g16: LineSegment [constr] StartX=-66 StartY=117.5 StartZ=0 EndX=-66 EndY=113.25 EndZ=0
    g17: LineSegment [constr] StartX=-66 StartY=109 StartZ=0 EndX=-66 EndY=104.75 EndZ=0
    g18: LineSegment [constr] StartX=-66 StartY=100.5 StartZ=0 EndX=-66 EndY=96.25 EndZ=0
  constraints (54):
    c: Coincident(g0,g1)
    c: Coincident(g1,g2)
    c: Coincident(g2,g3)
    c: Coincident(g3,g0)
    c: Horizontal(g0)
    c: Horizontal(g2)
    c: Vertical(g1)
    c: Vertical(g3)
    c: Coincident(g4,g5)
    c: Coincident(g5,g6)
    c: Coincident(g6,g7)
    c: Coincident(g7,g4)
    c: Horizontal(g4)
    c: Horizontal(g6)
    c: Vertical(g5)
    c: Vertical(g7)
    c: Coincident(g8,g9)
    c: Coincident(g9,g10)
    c: Coincident(g10,g11)
    c: Coincident(g11,g8)
    c: Horizontal(g8)
    c: Horizontal(g10)
    c: Vertical(g9)
    c: Vertical(g11)
    c: Coincident(g12,g13)
    c: Coincident(g13,g14)
    c: Coincident(g14,g15)
    c: Coincident(g15,g12)
    c: Horizontal(g12)
    c: Horizontal(g14)
    c: Vertical(g13)
    c: Vertical(g15)
    c: Coincident(g16,g2)
    c: Coincident(g16,g4)
    c: Coincident(g17,g6)
    c: Coincident(g17,g8)
    c: Coincident(g18,g10)
    c: Coincident(g18,g12)
    c: Vertical(g18)
    c: Vertical(g17)
    c: Vertical(g16)
    c: Equal(g3,g16)
    c: Equal(g16,g7)
    c: Equal(g7,g17)
    c: Equal(g17,g11)
    c: Equal(g11,g18)
    c: Equal(g18,g15)
    c: Distance(g3) = 4.25
    c: Distance(g0) = 60
    c: DistanceY(g-1,g13) = 92
    c: Equal(g2,g6)
    c: Equal(g6,g10)
    c: Equal(g10,g14)
    c: DistanceX(g-1,g13) = -6
FEATURE [PartDesign::Pad] Pad004
  Length = 45
  Length2 = 100
  Placement = pos=(-40,0,0) rot=(0.57735,-0.57735,-0.57735;2.0944rad)
  Reversed = true
  Sketch = -> Sketch009
  Type = 0
FEATURE [Sketcher::SketchObject] Sketch010
  Placement = pos=(-1,0,0) rot=(0.57735,0.57735,0.57735;2.0944rad)
  sketch-geometry (4):
    g0: LineSegment StartX=-7.05302 StartY=102.221 StartZ=0 EndX=-7.05302 EndY=138.84 EndZ=0
    g1: LineSegment StartX=-7.05302 StartY=138.84 StartZ=0 EndX=-42.2607 EndY=142.654 EndZ=0
    g2: LineSegment StartX=-42.2607 StartY=142.654 StartZ=0 EndX=-42.2607 EndY=119.265 EndZ=0
    g3: LineSegment StartX=-42.2607 StartY=119.265 StartZ=0 EndX=-7.05302 EndY=102.221 EndZ=0
  constraints (6):
    c: Coincident(g0,g1)
    c: Coincident(g1,g2)
    c: Coincident(g2,g3)
    c: Coincident(g0,g3)
    c: Vertical(g0)
    c: Vertical(g2)
FEATURE [PartDesign::Pad] Pad005
  Length = 42
  Length2 = 100
  Placement = pos=(-1,0,0) rot=(0.57735,0.57735,0.57735;2.0944rad)
  Sketch = -> Sketch010
  Type = 0
FEATURE [Part::MultiFuse] Fusion045
  Placement = pos=(23,4.5,120) rot=(0,0.707107,-0.707107;3.14159rad)
  Shapes = -> [Part__Feature,Part__Feature004,Part__Feature005]
FEATURE [Part::FeaturePython] Clone007  label="Clone of Fusion045"  # Draft clone (typed FeaturePython)
  Objects = -> [Fusion045]
  Placement = pos=(23,67.5,120) rot=(0,0.707107,0.707107;3.14159rad)
  Scale = (1,1,1)
FEATURE [Part::FeaturePython] Clone008  label="Clone of Fusion157"  # Draft clone (typed FeaturePython)
  Objects = -> [Fusion045]
  Placement = pos=(23,4.5,120) rot=(0,0.707107,-0.707107;3.14159rad)
  Scale = (1,1,1)
FEATURE [Sketcher::SketchObject] Sketch011
  Placement = pos=(-0.25,-35,0) rot=(1,0,0;1.5708rad)
  sketch-geometry (7):
    g0: Circle CenterX=37 CenterY=120 CenterZ=0 NormalX=0 NormalY=0 NormalZ=1 Radius=1.2
    g1: Circle CenterX=9.5 CenterY=120 CenterZ=0 NormalX=0 NormalY=0 NormalZ=1 Radius=1.2
    g2: LineSegment StartX=35.25 StartY=126.5 StartZ=0 EndX=11.25 EndY=126.5 EndZ=0
    g3: LineSegment StartX=11.25 StartY=126.5 StartZ=0 EndX=11.25 EndY=113.5 EndZ=0
    g4: LineSegment StartX=11.25 StartY=113.5 StartZ=0 EndX=35.25 EndY=113.5 EndZ=0
    g5: LineSegment StartX=35.25 StartY=113.5 StartZ=0 EndX=35.25 EndY=126.5 EndZ=0
    g6: LineSegment [constr] StartX=9.5 StartY=120 StartZ=0 EndX=37 EndY=120 EndZ=0
  constraints (20):
    c: Coincident(g2,g3)
    c: Coincident(g3,g4)
    c: Coincident(g4,g5)
    c: Coincident(g5,g2)
    c: Horizontal(g2)
    c: Horizontal(g4)
    c: Vertical(g3)
    c: Vertical(g5)
    c: Distance(g2) = 24
    c: Distance(g5) = 13
    c: Radius(g1) = 1.2
    c: Equal(g1,g0)
    c: Coincident(g0,g6)
    c: Coincident(g1,g6)
    c: Distance(g6) = 27.5
    c: Horizontal(g6)
    c: DistanceX(g-1,g1) = 9.5
    c: DistanceY(g1) = 120
    c: DistanceY(g1,g3) = -6.5
    c: DistanceX(g1,g2) = 1.75
FEATURE [PartDesign::Pad] Pad006
  Length = 140
  Length2 = 100
  Placement = pos=(-0.25,-35,0) rot=(1,0,0;1.5708rad)
  Reversed = true
  Sketch = -> Sketch011
  Type = 0
FEATURE [Part::FeaturePython] Clone009  label="Clone of Fusion158"  # Draft clone (typed FeaturePython)
  Objects = -> [Fusion045]
  Placement = pos=(18.5,-32,120) rot=(0.707107,0,0.707107;3.14159rad)
  Scale = (1,1,1)
FEATURE [Sketcher::SketchObject] Sketch012
  Placement = pos=(3,-12,-1) rot=(0.57735,0.57735,0.57735;2.0944rad)
  sketch-geometry (4):
    g0: LineSegment StartX=-4.88207 StartY=101.941 StartZ=0 EndX=-4.88207 EndY=138.56 EndZ=0
    g1: LineSegment StartX=-4.88207 StartY=138.56 StartZ=0 EndX=-40.5711 EndY=142.374 EndZ=0
    g2: LineSegment StartX=-40.5711 StartY=142.374 StartZ=0 EndX=-40.5711 EndY=120.688 EndZ=0
    g3: LineSegment StartX=-40.5711 StartY=120.688 StartZ=0 EndX=-4.88207 EndY=101.941 EndZ=0
  constraints (6):
    c: Coincident(g0,g1)
    c: Coincident(g1,g2)
    c: Coincident(g2,g3)
    c: Coincident(g0,g3)
    c: Vertical(g0)
    c: Vertical(g2)
FEATURE [PartDesign::Pad] Pad007
  Length = 34
  Length2 = 100
  Placement = pos=(3,-12,-1) rot=(0.57735,0.57735,0.57735;2.0944rad)
  Sketch = -> Sketch012
  Type = 0
FEATURE [Part::Cut] Cut085
  Base = -> Pad005
  Tool = -> Pad007
FEATURE [Part::Cylinder] Cylinder056  label="Cilindro"
  Angle = 360
  Height = 10
  Placement = pos=(17.25,-4,120) rot=(1,0,0;1.5708rad)
  Radius = 10
FEATURE [Part::Cut] Cut086
  Base = -> Cut085
  Tool = -> Cylinder056
FEATURE [Part::Cylinder] Cylinder057  label="Cilindro001"
  Angle = 360
  Height = 13
  Placement = pos=(17.25,-6,120) rot=(1,0,0;1.5708rad)
  Radius = 3
FEATURE [Part::Cut] Cut087
  Base = -> Cut086
  Tool = -> Cylinder057
FEATURE [Part::Chamfer] Chamfer104
  Base = -> Cut087
  Edges = 1 edges r=5: [Edge10]
FEATURE [Part::Cylinder] Cylinder058  label="Cilindro002"
  Angle = 360
  Height = 22
  Placement = pos=(20.25,-32,125.75) rot=(0,1,0;1.5708rad)
  Radius = 3
FEATURE [Part::Cut] Cut088
  Base = -> Chamfer104
  Tool = -> Cylinder058
FEATURE [Part::Cylinder] Cylinder059  label="Cilindro003"
  Angle = 360
  Height = 22
  Placement = pos=(20.25,-34,132.75) rot=(0,1,0;1.5708rad)
  Radius = 1.25
FEATURE [Part::Cylinder] Cylinder060  label="Cilindro004"
  Angle = 360
  Height = 22
  Placement = pos=(20.25,-30,118.75) rot=(0,1,0;1.5708rad)
  Radius = 1.25
FEATURE [Part::Cylinder] Cylinder061  label="Cilindro005"
  Angle = 360
  Height = 22
  Placement = pos=(20.25,-38,124.25) rot=(0,1,0;1.5708rad)
  Radius = 1.25
FEATURE [Part::Cylinder] Cylinder062  label="Cilindro006"
  Angle = 360
  Height = 22
  Placement = pos=(20.25,-26,127.25) rot=(0,1,0;1.5708rad)
  Radius = 1.25
FEATURE [Part::MultiFuse] Fusion046
  Shapes = -> [Cylinder059,Cylinder061,Cylinder062,Cylinder060]
FEATURE [Part::Cylinder] Cylinder063  label="Cilindro007"
  Angle = 360
  Height = 22
  Placement = pos=(20.25,-34,132.75) rot=(0,1,0;1.5708rad)
  Radius = 1.25
FEATURE [Part::Cylinder] Cylinder064  label="Cilindro008"
  Angle = 360
  Height = 22
  Placement = pos=(20.25,-30,118.75) rot=(0,1,0;1.5708rad)
  Radius = 1.25
FEATURE [Part::Cylinder] Cylinder065  label="Cilindro009"
  Angle = 360
  Height = 22
  Placement = pos=(20.25,-38,124.25) rot=(0,1,0;1.5708rad)
  Radius = 1.25
FEATURE [Part::Cylinder] Cylinder066  label="Cilindro010"
  Angle = 360
  Height = 22
  Placement = pos=(20.25,-26,127.25) rot=(0,1,0;1.5708rad)
  Radius = 1.25
FEATURE [Part::MultiFuse] Fusion047
  Placement = pos=(114.108,21,33.6462) rot=(0.280624,-0.280624,-0.917878;1.65638rad)
  Shapes = -> [Cylinder063,Cylinder065,Cylinder066,Cylinder064]
FEATURE [Part::Cut] Cut089
  Base = -> Cut088
  Tool = -> Fusion047
FEATURE [Part::Cut] Cut090
  Base = -> Cut089
  Tool = -> Fusion046
FEATURE [Part::Cylinder] Cylinder067  label="Cilindro011"
  Angle = 360
  Height = 22
  Placement = pos=(-4.75,-32,125.75) rot=(0,1,0;1.5708rad)
  Radius = 1.75
FEATURE [Part::Cut] Cut091
  Base = -> Cut090
  Tool = -> Cylinder067
FEATURE [Part::Box] Box049  label="Cubo"
  Height = 4
  Length = 14
  Placement = pos=(11,-6.5,109) rot=(0,0,1;0rad)
  Width = 3
FEATURE [Part::MultiFuse] Fusion048
  Shapes = -> [Cut082,Box049]
FEATURE [Part::Box] Box050  label="Cubo001"
  Height = 4
  Length = 14
  Placement = pos=(11,-6.5,127) rot=(0,0,1;0rad)
  Width = 3
FEATURE [Part::MultiFuse] Fusion049
  Shapes = -> [Fusion048,Box050]
FEATURE [Part::Box] Box051  label="Cubo002"
  Height = 4
  Length = 14
  Placement = pos=(11,75.5,127) rot=(0,0,1;0rad)
  Width = 3
FEATURE [Part::Box] Box052  label="Cubo003"
  Height = 4
  Length = 14
  Placement = pos=(11,75.5,109) rot=(0,0,1;0rad)
  Width = 3
FEATURE [Part::MultiFuse] Fusion050
  Shapes = -> [Box052,Box051,Fusion049]
FEATURE [Part::MultiFuse] Fusion051
  Shapes = -> [Pad004,Pad006]
FEATURE [Part::Cut] Cut092
  Base = -> Fusion050
  Tool = -> Fusion051
FEATURE [Part::Fillet] Fillet018013002
  Base = -> Cut092
  Edges = 8 edges r=1: [Edge2,Edge4,Edge56,Edge59,Edge207,Edge210,Edge226,Edge228]
FEATURE [Part::Chamfer] Chamfer105
  Base = -> Cut091
  Edges = 1 edges r=5: [Edge33]
FEATURE [Part::FeaturePython] Clone010  label="Clone of Chamfer105"  # Draft clone (typed FeaturePython)
  Objects = -> [Chamfer105]
  Scale = (1,1,1)
FEATURE [Part::Mirroring] Part__Mirroring007008  label="Clone of Chamfer105 (Mirror #10)"
  Base = (0,0,0)
  Normal = (0,1,0)
  Placement = pos=(0,72,0) rot=(0,0,1;0rad)
  Source = -> Clone010
FEATURE [Sketcher::SketchObject] Sketch013
  Placement = pos=(0,0,195) rot=(0,0,1;0rad)
  sketch-geometry (8):
    g0: LineSegment StartX=-39 StartY=19 StartZ=0 EndX=-39 EndY=23 EndZ=0
    g1: LineSegment StartX=-39 StartY=23 StartZ=0 EndX=-14 EndY=23 EndZ=0
    g2: LineSegment StartX=-14 StartY=23 StartZ=0 EndX=-14 EndY=-9 EndZ=0
    g3: LineSegment StartX=-14 StartY=-9 StartZ=0 EndX=-39 EndY=-9 EndZ=0
    g4: LineSegment StartX=-39 StartY=-9 StartZ=0 EndX=-39 EndY=-5 EndZ=0
    g5: LineSegment StartX=-39 StartY=-5 StartZ=0 EndX=-18 EndY=-5 EndZ=0
    g6: LineSegment StartX=-18 StartY=19 StartZ=0 EndX=-39 EndY=19 EndZ=0
    g7: LineSegment StartX=-18 StartY=19 StartZ=0 EndX=-18 EndY=-5 EndZ=0
  constraints (24):
    c: Vertical(g0)
    c: Coincident(g0,g1)
    c: Horizontal(g1)
    c: Coincident(g1,g2)
    c: Vertical(g2)
    c: Coincident(g2,g3)
    c: Coincident(g3,g4)
    c: Vertical(g4)
    c: Coincident(g4,g5)
    c: Horizontal(g5)
    c: Coincident(g6,g0)
    c: Horizontal(g6)
    c: Horizontal(g3)
    c: Equal(g4,g0)
    c: Distance(g0) = 4
    c: Distance(g1) = 25
    c: DistanceY(g-1,g1) = 23
    c: DistanceX(g-1,g1) = -14
    c: Distance(g2) = 32
    c: Equal(g3,g1)
    c: DistanceX(g5,g2) = 4
    c: DistanceX(g6,g1) = 4
    c: Coincident(g7,g6)
    c: Coincident(g7,g5)
FEATURE [PartDesign::Pad] Pad008
  Length = 13
  Length2 = 100
  Placement = pos=(0,0,195) rot=(0,0,1;0rad)
  Sketch = -> Sketch013
  Type = 0
FEATURE [Part::Chamfer] Chamfer106
  Base = -> Pad008
  Edges = 2 edges r=7: [Edge5,Edge20]
FEATURE [Part::Cylinder] Cylinder068  label="Cylinder098"
  Angle = 360
  Height = 20
  Placement = pos=(-33,-7,202) rot=(0,-1,0;1.5708rad)
  Radius = 1
FEATURE [Part::Cylinder] Cylinder069  label="Cylinder099"
  Angle = 360
  Height = 20
  Placement = pos=(-33,21,202) rot=(0,-1,0;1.5708rad)
  Radius = 1
FEATURE [Part::MultiFuse] Fusion052
  Placement = pos=(5,0,0) rot=(0,0,1;0rad)
  Shapes = -> [Cylinder068,Cylinder069]
FEATURE [Part::Cut] Cut093
  Base = -> Chamfer106
  Tool = -> Fusion052
FEATURE [Part::Cylinder] Cylinder070
  Angle = 360
  Height = 20
  Placement = pos=(-7,12.8,202) rot=(0,-1,0;1.5708rad)
  Radius = 1.75
FEATURE [Part::Prism] Prism
  Circumradius = 3.3
  Height = 10
  Placement = pos=(-16,12.8,202) rot=(0,-1,0;1.5708rad)
  Polygon = 6
FEATURE [Part::MultiFuse] Fusion053
  Shapes = -> [Prism,Cylinder070]
FEATURE [Part::Cut] Cut094
  Base = -> Cut093
  Placement = pos=(34,4,-65) rot=(0,0,-1;1.5708rad)
  Tool = -> Fusion053
FEATURE [Part::Box] Box053  label="Cube077"
  Height = 15
  Length = 7
  Placement = pos=(16,29,120) rot=(0,0,-1;1.5708rad)
  Width = 17
FEATURE [Part::Chamfer] Chamfer107
  Base = -> Cut094
  Edges = 1 edges r=2: [Edge4]
  Placement = pos=(-13,0,0) rot=(0,0,1;0rad)
FEATURE [Part::Cut] Cut095
  Base = -> Fillet018013002
  Tool = -> Box053
FEATURE [Part::MultiFuse] Fusion054
  Shapes = -> [Cut095,Chamfer107]
FEATURE [Part::FeaturePython] Clone011  label="Clone of Clone of Fusion158"  # Draft clone (typed FeaturePython)
  Objects = -> [Clone009]
  Placement = pos=(18.5,104,120) rot=(0.707107,0,0.707107;3.14159rad)
  Scale = (1,1,1)
FEATURE [Part::Box] Box054  label="Cubo004"
  Height = 56
  Length = 19
  Placement = pos=(4,98,80) rot=(0,0,1;0rad)
  Width = 15
FEATURE [Sketcher::SketchObject] Sketch014
  Placement = pos=(0,93,0) rot=(0,0.707107,0.707107;3.14159rad)
  sketch-geometry (4):
    g0: LineSegment StartX=-36.0792 StartY=39.6394 StartZ=0 EndX=-28.646 EndY=87.1961 EndZ=0
    g1: LineSegment StartX=-28.646 StartY=87.1961 StartZ=0 EndX=6.55476 EndY=92.8148 EndZ=0
    g2: LineSegment StartX=6.55476 StartY=92.8148 StartZ=0 EndX=-17.4144 EndY=36.7221 EndZ=0
    g3: LineSegment StartX=-17.4144 StartY=36.7221 StartZ=0 EndX=-36.0792 EndY=39.6394 EndZ=0
  constraints (5):
    c: Coincident(g0,g1)
    c: Coincident(g1,g2)
    c: Coincident(g2,g3)
    c: Coincident(g3,g0)
    c: Perpendicular(g3,g0)
FEATURE [PartDesign::Pad] Pad009
  Length = 25
  Length2 = 100
  Placement = pos=(0,93,0) rot=(0,0.707107,0.707107;3.14159rad)
  Sketch = -> Sketch014
  Type = 0
FEATURE [Part::Box] Box055  label="Cubo005"
  Height = 56
  Length = 20
  Placement = pos=(3.5,97.5,79.5) rot=(0,0,1;0rad)
  Width = 16
FEATURE [Part::Cut] Cut096
  Base = -> Pad009
  Tool = -> Box055
FEATURE [Part::Cylinder] Cylinder071  label="Cilindro012"
  Angle = 360
  Height = 32
  Placement = pos=(8,90,84) rot=(-1,0,0;1.5708rad)
  Radius = 1.75
FEATURE [Part::Cylinder] Cylinder072  label="Cilindro013"
  Angle = 360
  Height = 32
  Placement = pos=(18,90,84) rot=(-1,0,0;1.5708rad)
  Radius = 1.75
FEATURE [Part::MultiFuse] Fusion055
  Shapes = -> [Cylinder072,Cylinder071]
FEATURE [Part::Cut] Cut097
  Base = -> Cut096
  Tool = -> Fusion055
FEATURE [Part::Cylinder] Cylinder073  label="Cilindro014"
  Angle = 360
  Height = 32
  Placement = pos=(8,90,84) rot=(-1,0,0;1.5708rad)
  Radius = 1.75
FEATURE [Part::Cylinder] Cylinder074  label="Cilindro015"
  Angle = 360
  Height = 32
  Placement = pos=(18,90,84) rot=(-1,0,0;1.5708rad)
  Radius = 1.75
FEATURE [Part::MultiFuse] Fusion056
  Shapes = -> [Cylinder074,Cylinder073]
FEATURE [Part::Cut] Cut098
  Base = -> Box054
  Tool = -> Fusion056
FEATURE [Sketcher::SketchObject] Sketch015
  Placement = pos=(38,-16,143.25) rot=(0,1,0;1.5708rad)
  sketch-geometry (7):
    g0: Circle CenterX=37 CenterY=120 CenterZ=0 NormalX=0 NormalY=0 NormalZ=1 Radius=1
    g1: Circle CenterX=9.5 CenterY=120 CenterZ=0 NormalX=0 NormalY=0 NormalZ=1 Radius=1
    g2: LineSegment StartX=35.25 StartY=126.5 StartZ=0 EndX=11.25 EndY=126.5 EndZ=0
    g3: LineSegment StartX=11.25 StartY=126.5 StartZ=0 EndX=11.25 EndY=113.5 EndZ=0
    g4: LineSegment StartX=11.25 StartY=113.5 StartZ=0 EndX=35.25 EndY=113.5 EndZ=0
    g5: LineSegment StartX=35.25 StartY=113.5 StartZ=0 EndX=35.25 EndY=126.5 EndZ=0
    g6: LineSegment [constr] StartX=9.5 StartY=120 StartZ=0 EndX=37 EndY=120 EndZ=0
  constraints (20):
    c: Coincident(g2,g3)
    c: Coincident(g3,g4)
    c: Coincident(g4,g5)
    c: Coincident(g5,g2)
    c: Horizontal(g2)
    c: Horizontal(g4)
    c: Vertical(g3)
    c: Vertical(g5)
    c: Distance(g2) = 24
    c: Distance(g5) = 13
    c: Radius(g1) = 1
    c: Equal(g1,g0)
    c: Coincident(g0,g6)
    c: Coincident(g1,g6)
    c: Distance(g6) = 27.5
    c: Horizontal(g6)
    c: DistanceX(g-1,g1) = 9.5
    c: DistanceY(g1) = 120
    c: DistanceY(g1,g3) = -6.5
    c: DistanceX(g1,g2) = 1.75
FEATURE [PartDesign::Pad] Pad010
  Length = 30
  Length2 = 100
  Placement = pos=(38,-16,143.25) rot=(0,1,0;1.5708rad)
  Reversed = true
  Sketch = -> Sketch015
  Type = 0
FEATURE [Part::Cut] Cut099
  Base = -> Cut098
  Tool = -> Pad010
FEATURE [Part::Chamfer] Chamfer108
  Base = -> Cut099
  Edges = 1 edges r=3: [Edge14]
FEATURE [Part::Cylinder] Cylinder075  label="Cilindro016"
  Angle = 360
  Height = 32
  Placement = pos=(-5,104,125.85) rot=(-0.57735,0.57735,-0.57735;2.0944rad)
  Radius = 1.75
FEATURE [Part::Prism] Prism001  label="Prisma"
  Circumradius = 3.3
  Height = 10
  Placement = pos=(6,104,125.85) rot=(-0.57735,0.57735,-0.57735;2.0944rad)
  Polygon = 6
FEATURE [Part::MultiFuse] Fusion057
  Shapes = -> [Prism001,Cylinder075]
FEATURE [Part::Cut] Cut100
  Base = -> Chamfer108
  Tool = -> Fusion057
FEATURE [Part::Prism] Prism002  label="Prisma001"
  Circumradius = 3.3
  Height = 10
  Placement = pos=(18,85,84) rot=(-1,0,0;1.5708rad)
  Polygon = 6
FEATURE [Part::Cylinder] Cylinder076  label="Cilindro017"
  Angle = 360
  Height = 32
  Placement = pos=(18,116,84) rot=(-1,0,0;1.5708rad)
  Radius = 3
FEATURE [Part::Prism] Prism003  label="Prisma002"
  Circumradius = 3.3
  Height = 10
  Placement = pos=(8,85,84) rot=(-1,0,0;1.5708rad)
  Polygon = 6
FEATURE [Part::MultiFuse] Fusion058
  Shapes = -> [Prism003,Prism002]
FEATURE [Part::Cut] Cut101
  Base = -> Cut097
  Tool = -> Fusion058
FEATURE [Part::Cylinder] Cylinder077  label="Cilindro018"
  Angle = 360
  Height = 32
  Placement = pos=(8,116,84) rot=(-1,0,0;1.5708rad)
  Radius = 3
FEATURE [Part::MultiFuse] Fusion059
  Shapes = -> [Cylinder076,Cylinder077]
FEATURE [Part::Cut] Cut102
  Base = -> Cut101
  Tool = -> Fusion059
FEATURE [Part::Chamfer] Chamfer109
  Base = -> Cut102
  Edges = 1 edges r=5: [Edge10]
FEATURE [Part::FeaturePython] Clone012  label="Clone of Cut100"  # Draft clone (typed FeaturePython)
  Objects = -> [Cut100]
  Scale = (1,1,1)
FEATURE [Part::FeaturePython] Clone013  label="Clone of Chamfer109"  # Draft clone (typed FeaturePython)
  Objects = -> [Chamfer109]
  Scale = (1,1,1)
FEATURE [Part::Mirroring] Part__Mirroring007009  label="Clone of Cut100 (Mirror #11)"
  Base = (0,0,0)
  Normal = (0,1,0)
  Placement = pos=(0,72,0) rot=(0,0,1;0rad)
  Source = -> Clone012
FEATURE [Part::Mirroring] Part__Mirroring007010  label="Clone of Chamfer109 (Mirror #12)"
  Base = (0,0,0)
  Normal = (0,1,0)
  Placement = pos=(0,72,0) rot=(0,0,1;0rad)
  Source = -> Clone013
FEATURE [Part::FeaturePython] Clone014  label="Clone of pie-D"  # Draft clone (typed FeaturePython)
  Objects = -> [Cut039]
  Placement = pos=(0,0,1) rot=(0,0,1;0rad)
  Scale = (1,1,1)
FEATURE [Part::Box] Box056  label="Cubo006"
  Height = 4
  Length = 72
  Placement = pos=(-15,-29,-2) rot=(0,0,1;0rad)
  Width = 58
FEATURE [Part::MultiFuse] Fusion060
  Shapes = -> [Clone014,Box056]
FEATURE [Part::Chamfer] Chamfer110
  Base = -> Fusion060
  Edges = 4 edges: [Edge177 r=7,Edge181 r=12,Edge186 r=7,Edge190 r=7]
FEATURE [Part::Mirroring] Part__Mirroring007011  label="Chamfer110 (Mirror #13)"
  Base = (0,0,0)
  Normal = (0,1,0)
  Placement = pos=(0,72,0) rot=(0,0,1;0rad)
  Source = -> Chamfer110
FEATURE [Part::Box] Box057  label="Cubo007"
  Height = 53
  Length = 35
  Placement = pos=(50,1,73) rot=(0,0,1;0rad)
  Width = 70
FEATURE [Part::Cut] Cut103
  Base = -> Fusion054
  Tool = -> Box057
FEATURE [Part::Feature] Part__Feature026  label="Board"
  Placement = pos=(0,0,-0.41148) rot=(0,0,1;0rad)
  shape: bbox 35.02 x 16.02 x 0.4115 mm, 46 faces (baked)
FEATURE [Part::Feature] Part__Feature027  label="ah1862"
  Placement = pos=(4.99992,8.00005,3) rot=(0.707107,-0.707107,0;3.14159rad)
  shape: bbox 11.02 x 13.9 x 9.101 mm, 290 faces (baked)
FEATURE [Part::Feature] Part__Feature028  label="c-0103634-02-u-3d"
  Placement = pos=(34.573,7.99996,2.98) rot=(0.57735,0.57735,0.57735;2.0944rad)
  shape: bbox 13.59 x 10.16 x 10.29 mm, 129 faces (baked)
FEATURE [Part::Feature] Part__Feature029  label="User_Library-LED_SMD0603"
  Placement = pos=(14.6351,7.9999,0) rot=(0,0,-1;1.5708rad)
  shape: bbox 1.6 x 0.725 x 0.3 mm, 10 faces (baked)
FEATURE [Part::Feature] Part__Feature030  label="User_Library-LED_SMD0604"
  Placement = pos=(14.6351,7.9999,0) rot=(0,0,-1;1.5708rad)
  shape: bbox 1 x 0.725 x 0.35 mm, 6 faces (baked)
FEATURE [Part::Feature] Part__Feature031  label="User_Library-LED_SMD0605"
  Placement = pos=(14.6351,7.9999,0) rot=(0,0,-1;1.5708rad)
  shape: bbox 0.1601 x 0.1489 x 0.075 mm, 6 faces (baked)
FEATURE [Part::Feature] Part__Feature032  label="User_Library-LED_SMD0606"
  Placement = pos=(14.6351,7.9999,0) rot=(0,0,-1;1.5708rad)
  shape: bbox 0.275 x 0.65 x 0.35 mm, 14 faces (baked)
FEATURE [Part::Feature] Part__Feature033  label="User_Library-LED_SMD0607"
  Placement = pos=(14.6351,7.9999,0) rot=(0,0,-1;1.5708rad)
  shape: bbox 0.275 x 0.65 x 0.35 mm, 14 faces (baked)
FEATURE [Part::Feature] Part__Feature034  label="RES_0603L"
  Placement = pos=(16.99,8,0) rot=(0,0,1;0rad)
  shape: bbox 1.6 x 0.8 x 0.4 mm, 36 faces (baked)
FEATURE [Part::MultiFuse] Fusion061
  Placement = pos=(60,66,105) rot=(0,0,1;3.14159rad)
  Shapes = -> [Part__Feature026,Part__Feature033,Part__Feature034,Part__Feature029,Part__Feature030,Part__Feature032,Part__Feature031,Part__Feature027,Part__Feature028]
FEATURE [Part::FeaturePython] Clone015  label="Clone of Fusion061"  # Draft clone (typed FeaturePython)
  Objects = -> [Fusion061]
  Placement = pos=(60,6,111) rot=(0,1,0;3.14159rad)
  Scale = (1,1,1)
FEATURE [Part::Box] Box058  label="Cubo008"
  Height = 19
  Length = 10
  Placement = pos=(39,-3,111.5) rot=(0,0,1;0rad)
  Width = 25
FEATURE [Part::FeaturePython] Clone016  label="Clone of Cubo008"  # Draft clone (typed FeaturePython)
  Objects = -> [Box058]
  Placement = pos=(39,50,111.5) rot=(0,0,1;0rad)
  Scale = (1,1,1)
FEATURE [Part::Cylinder] Cylinder078  label="Cilindro019"
  Angle = 360
  Height = 42
  Placement = pos=(44,63,97) rot=(0,0,1;0rad)
  Radius = 1.3
FEATURE [Part::FeaturePython] Clone017  label="Clone of Cilindro019"  # Draft clone (typed FeaturePython)
  Objects = -> [Cylinder078]
  Placement = pos=(44,53,97) rot=(0,0,1;0rad)
  Scale = (1,1,1)
FEATURE [Part::FeaturePython] Clone018  label="Clone of Clone of Cilindro019"  # Draft clone (typed FeaturePython)
  Objects = -> [Clone017]
  Placement = pos=(44,9,98) rot=(0,0,1;0rad)
  Scale = (1,1,1)
FEATURE [Part::FeaturePython] Clone019  label="Clone of Cilindro020"  # Draft clone (typed FeaturePython)
  Objects = -> [Cylinder078]
  Placement = pos=(44,19,98) rot=(0,0,1;0rad)
  Scale = (1,1,1)
FEATURE [Part::Cut] Cut104
  Base = -> Box058
  Tool = -> Clone018
FEATURE [Part::Cut] Cut105
  Base = -> Cut104
  Tool = -> Clone019
FEATURE [Part::Cut] Cut106
  Base = -> Clone016
  Tool = -> Clone017
FEATURE [Part::Cut] Cut107
  Base = -> Cut106
  Tool = -> Cylinder078
FEATURE [Part::MultiFuse] Fusion062
  Shapes = -> [Cut107,Cut103,Cut105]
FEATURE [Part::Box] Box060  label="Cubo010"
  Height = 52
  Length = 8
  Width = 69
FEATURE [Part::Box] Box061  label="Cubo011"
  Height = 48
  Length = 8
  Width = 65
FEATURE [Part::Cut] Cut108
  Base = -> Box060
  Tool = -> Box061
FEATURE [Sketcher::SketchObject] Sketch016
  ExternalGeometry = -> [Cut108]
  Placement = pos=(0,70.5,0) rot=(0,0.707107,0.707107;3.14159rad)
  Support = -> Cut108 [Face5]
  sketch-geometry (5):
    g0: LineSegment StartX=-52 StartY=77.5 StartZ=0 EndX=-56 EndY=77.5 EndZ=0
    g1: LineSegment StartX=-56 StartY=77.5 StartZ=0 EndX=-56 EndY=84.5 EndZ=0
    g2: LineSegment StartX=-56 StartY=84.5 StartZ=0 EndX=-52 EndY=84.5 EndZ=0
    g3: ArcOfCircle CenterX=-52 CenterY=81 CenterZ=0 NormalX=0 NormalY=0 NormalZ=1 Radius=3.5 StartAngle=4.71239 EndAngle=7.85398
    g4: Circle CenterX=-52 CenterY=81 CenterZ=0 NormalX=0 NormalY=0 NormalZ=1 Radius=1.4
  constraints (15):
    c: Coincident(g0,g1)
    c: Coincident(g1,g2)
    c: Horizontal(g0)
    c: Horizontal(g2)
    c: Vertical(g1)
    c: PointOnObject(g0,g-3)
    c: DistanceY(g0,g-3) = -4
    c: Coincident(g3,g0)
    c: Coincident(g3,g2)
    c: Tangent(g3,g2)
    c: Tangent(g0,g3)
    c: Coincident(g4,g3)
    c: Radius(g4) = 1.4
    c: Distance(g2) = 4
    c: Radius(g3) = 3.5
FEATURE [PartDesign::Pad] Pad011
  Length = 69
  Length2 = 100
  Reversed = true
  Sketch = -> Sketch016
  Type = 0
FEATURE [Part::Box] Box062  label="Cubo012"
  Height = 48
  Length = 20
  Width = 65
FEATURE [Part::Cut] Cut109
  Base = -> Pad011
  Placement = pos=(50,0,0) rot=(0,0,1;0rad)
  Tool = -> Box062
FEATURE [Part::Box] Box063  label="Cubo013"
  Height = 48
  Length = 20
  Placement = pos=(87,3.5,75.5) rot=(0,0,1;0rad)
  Width = 65
FEATURE [Part::Cut] Cut110
  Base = -> Cut109
  Tool = -> Box063
FEATURE [Part::Fillet] Fillet018013003
  Base = -> Cut110
  Edges = 2 edges r=1: [Edge14,Edge33]
FEATURE [Part::Fillet] Fillet018013004
  Base = -> Fillet018013003
  Edges = 2 edges r=2.5: [Edge21,Edge37]
FEATURE [Part::Fillet] Fillet018013005
  Base = -> Fillet018013004
  Edges = 8 edges r=1: [Edge68,Edge69,Edge70,Edge80,Edge81,Edge82,Edge83,Edge85]
FEATURE [Part::Cylinder] Cylinder079  label="Cilindro020"
  Angle = 360
  Height = 500
  Placement = pos=(52,136,81) rot=(1,0,0;1.5708rad)
  Radius = 1
FEATURE [Part::Fillet] Fillet018013006
  Base = -> Fillet018013005
  Edges = 4 edges r=2: [Edge25,Edge29,Edge33,Edge44]
FEATURE [Part::Chamfer] Chamfer111
  Base = -> Fillet018013006
  Edges = 1 edges r=1.5: [Edge26]
  Placement = pos=(-50,0,0) rot=(0,0,1;0rad)
FEATURE [Part::Cut] Cut111
  Base = -> Fusion062
  Tool = -> Cylinder079
FEATURE [Part::Fillet] Fillet018013007
  Base = -> Cut111
  Edges = 4 edges r=1.5: [Edge225,Edge226,Edge230,Edge232]
FEATURE [Part::Fillet] Fillet018013008
  Base = -> Fillet018013007
  Edges = 6 edges r=3: [Edge339,Edge344,Edge416,Edge422,Edge443,Edge449]
FEATURE [Part::Cylinder] Cylinder080  label="Cilindro021"
  Angle = 360
  Height = 80
  Placement = pos=(65,-33,30) rot=(0,1,0;1.5708rad)
  Radius = 6
FEATURE [Part::Box] Box064  label="Cubo014"
  Height = 60
  Length = 30
  Placement = pos=(145,-48,0) rot=(0,0,1;0rad)
  Width = 30
FEATURE [Part::Chamfer] Chamfer112
  Base = -> Box064
  Edges = 12 edges r=4: [Edge1,Edge2,Edge3,Edge4,Edge5,Edge6,Edge7,Edge8,Edge9,Edge10,Edge11,Edge12]
FEATURE [Part::Box] Box065  label="Cubo015"
  Height = 15
  Length = 40
  Placement = pos=(140,-53,-3) rot=(0,0,1;0rad)
  Width = 40
FEATURE [Part::Chamfer] Chamfer113
  Base = -> Box065
  Edges = 8 edges r=2: [Edge1,Edge2,Edge3,Edge5,Edge6,Edge7,Edge10,Edge12]
FEATURE [Part::MultiFuse] Fusion063
  Shapes = -> [Chamfer112,Chamfer113]
FEATURE [Part::Cylinder] Cylinder081  label="Cilindro022"
  Angle = 360
  Height = 8
  Placement = pos=(65,-33,30) rot=(0,1,0;1.5708rad)
  Radius = 7
FEATURE [Part::FeaturePython] Clone020  label="Clone of Cilindro022"  # Draft clone (typed FeaturePython)
  Objects = -> [Cylinder081]
  Placement = pos=(75,-33,30) rot=(0,1,0;1.5708rad)
  Scale = (1,1,1)
FEATURE [Part::FeaturePython] Clone021  label="Clone of Cilindro023"  # Draft clone (typed FeaturePython)
  Objects = -> [Cylinder081]
  Placement = pos=(85,-33,30) rot=(0,1,0;1.5708rad)
  Scale = (1,1,1)
FEATURE [Part::FeaturePython] Clone022  label="Clone of Cilindro024"  # Draft clone (typed FeaturePython)
  Objects = -> [Cylinder081]
  Placement = pos=(95,-33,30) rot=(0,1,0;1.5708rad)
  Scale = (1,1,1)
FEATURE [Part::FeaturePython] Clone023  label="Clone of Cilindro025"  # Draft clone (typed FeaturePython)
  Objects = -> [Cylinder081]
  Placement = pos=(105,-33,30) rot=(0,1,0;1.5708rad)
  Scale = (1,1,1)
FEATURE [Part::FeaturePython] Clone024  label="Clone of Cilindro026"  # Draft clone (typed FeaturePython)
  Objects = -> [Cylinder081]
  Placement = pos=(115,-33,30) rot=(0,1,0;1.5708rad)
  Scale = (1,1,1)
FEATURE [Part::FeaturePython] Clone025  label="Clone of Cilindro027"  # Draft clone (typed FeaturePython)
  Objects = -> [Cylinder081]
  Placement = pos=(125,-33,30) rot=(0,1,0;1.5708rad)
  Scale = (1,1,1)
FEATURE [Part::FeaturePython] Clone026  label="Clone of Cilindro028"  # Draft clone (typed FeaturePython)
  Objects = -> [Cylinder081]
  Placement = pos=(135,-33,30) rot=(0,1,0;1.5708rad)
  Scale = (1,1,1)
FEATURE [Part::MultiFuse] Fusion064
  Placement = pos=(-77,0,1) rot=(0,-1,0;0.174533rad)
  Shapes = -> [Cylinder080,Clone022,Clone026,Cylinder081,Clone023,Fusion063,Clone025,Clone020,Clone024,Clone021]
FEATURE [Part::Chamfer] Chamfer114
  Base = -> Fusion064
  Edges = 8 edges r=1: [Edge100,Edge104,Edge108,Edge112,Edge118,Edge119,Edge120,Edge121]
FEATURE [Part::Chamfer] Chamfer115
  Base = -> Chamfer114
  Edges = 8 edges r=2: [Edge33,Edge34,Edge35,Edge36,Edge37,Edge38,Edge39,Edge40]
FEATURE [Sketcher::SketchObject] Sketch017
  sketch-geometry (6):
    g0: LineSegment StartX=-45.9021 StartY=0 StartZ=0 EndX=-50 EndY=0 EndZ=0
    g1: LineSegment StartX=-50 StartY=0 StartZ=0 EndX=-50 EndY=-3 EndZ=0
    g2: LineSegment StartX=-50 StartY=-3 StartZ=0 EndX=-47 EndY=-3 EndZ=0
    g3: ArcOfCircle CenterX=0 CenterY=53.4706 CenterZ=0 NormalX=0 NormalY=0 NormalZ=1 Radius=73.4706 StartAngle=4.01827 EndAngle=4.71239
    g4: LineSegment StartX=0 StartY=-17 StartZ=0 EndX=0 EndY=-20 EndZ=0
    g5: ArcOfCircle CenterX=0 CenterY=53.4706 CenterZ=0 NormalX=0 NormalY=0 NormalZ=1 Radius=70.4706 StartAngle=4.00301 EndAngle=4.71239
  constraints (19):
    c: PointOnObject(g0,g-1)
    c: Coincident(g0,g1)
    c: Coincident(g1,g2)
    c: Horizontal(g2)
    c: Coincident(g3,g2)
    c: PointOnObject(g3,g-2)
    c: PointOnObject(g3,g-2)
    c: Coincident(g3,g4)
    c: Vertical(g1)
    c: Distance(g1) = 3
    c: DistanceX(g-1,g0) = -50
    c: DistanceY(g-1,g3) = -20
    c: Coincident(g0,g5)
    c: Coincident(g4,g5)
    c: Coincident(g3,g5)
    c: PointOnObject(g4,g-2)
    c: Distance(g2) = 3
    c: PointOnObject(g0,g-1)
    c: Distance(g4) = 3
FEATURE [PartDesign::Revolution] Revolution
  Angle = 360
  Axis = (0,1,0)
  Base = (0,0,0)
  ReferenceAxis = -> Sketch017 [V_Axis]
  Sketch = -> Sketch017
FEATURE [Sketcher::SketchObject] Sketch018
  sketch-geometry (3):
    g0: ArcOfCircle CenterX=0 CenterY=53.4707 CenterZ=0 NormalX=0 NormalY=0 NormalZ=1 Radius=70.4707 StartAngle=4.00301 EndAngle=4.71239
    g1: LineSegment StartX=-45.9021 StartY=0 StartZ=0 EndX=0 EndY=0 EndZ=0
    g2: LineSegment StartX=0 StartY=0 StartZ=0 EndX=0 EndY=-17 EndZ=0
  constraints (9):
    c: Distance(g1) = 45.9021
    c: Distance(g2) = 17
    c: Coincident(g0,g2)
    c: Coincident(g0,g1)
    c: Coincident(g1,g2)
    c: Coincident(g1,g-1)
    c: Vertical(g2)
    c: Horizontal(g1)
    c: Perpendicular(g0,g2)
FEATURE [PartDesign::Revolution] Revolution001
  Angle = 360
  Axis = (0,1,0)
  Base = (0,0,0)
  ReferenceAxis = -> Sketch018 [V_Axis]
  Sketch = -> Sketch018
FEATURE [Sketcher::SketchObject] Sketch019
  Placement = pos=(0,0,0) rot=(0,0.707107,0.707107;3.14159rad)
  Support = -> Revolution001 [Face2]
  sketch-geometry (19):
    g0: LineSegment StartX=-19 StartY=12 StartZ=0 EndX=21 EndY=12 EndZ=0
    g1: LineSegment StartX=21 StartY=7 StartZ=0 EndX=36 EndY=7 EndZ=0
    g2: ArcOfCircle CenterX=21 CenterY=8.03571 CenterZ=0 NormalX=0 NormalY=0 NormalZ=1 Radius=15.0357 StartAngle=4.71239 EndAngle=6.21425
    g3: LineSegment StartX=21 StartY=12 StartZ=0 EndX=21 EndY=7 EndZ=0
    g4: LineSegment StartX=21 StartY=-12 StartZ=0 EndX=21 EndY=-7 EndZ=0
    g5: LineSegment StartX=-24 StartY=14 StartZ=0 EndX=-29 EndY=14 EndZ=0
    g6: LineSegment StartX=-29 StartY=14 StartZ=0 EndX=-29 EndY=-14 EndZ=0
    g7: LineSegment StartX=-29 StartY=-14 StartZ=0 EndX=-24 EndY=-14 EndZ=0
    g8: LineSegment StartX=-24 StartY=-14 StartZ=0 EndX=-24 EndY=-10 EndZ=0
    g9: LineSegment StartX=-24 StartY=-10 StartZ=0 EndX=-19 EndY=-10 EndZ=0
    g10: LineSegment StartX=-19 StartY=10 StartZ=0 EndX=-24 EndY=10 EndZ=0
    g11: LineSegment StartX=-24 StartY=10 StartZ=0 EndX=-24 EndY=14 EndZ=0
    g12: LineSegment StartX=-19 StartY=-12 StartZ=0 EndX=-19 EndY=-10 EndZ=0
    g13: LineSegment StartX=-19 StartY=12 StartZ=0 EndX=-19 EndY=10 EndZ=0
    g14: ArcOfCircle CenterX=-8.00001 CenterY=-20 CenterZ=0 NormalX=0 NormalY=0 NormalZ=1 Radius=8 StartAngle=1.5708 EndAngle=3.14159
    g15: ArcOfCircle CenterX=9.99999 CenterY=-20 CenterZ=0 NormalX=0 NormalY=0 NormalZ=1 Radius=8 StartAngle=0 EndAngle=1.57079
    g16: LineSegment StartX=-16 StartY=-20 StartZ=0 EndX=18 EndY=-20 EndZ=0
    g17: LineSegment StartX=-8.00001 StartY=-12 StartZ=0 EndX=-19 EndY=-12 EndZ=0
    g18: LineSegment StartX=10 StartY=-12 StartZ=0 EndX=21 EndY=-12 EndZ=0
  constraints (62):
    c: Horizontal(g0)
    c: Coincident(g2,g1)
    c: Horizontal(g1)
    c: Coincident(g3,g0)
    c: Vertical(g4)
    c: Vertical(g3)
    c: Coincident(g1,g3)
    c: Coincident(g2,g4)
    c: Perpendicular(g2,g4)
    c: Equal(g3,g4)
    c: Distance(g1) = 15
    c: Distance(g4) = 5
    c: Distance(g0) = 40
    c: Horizontal(g5)
    c: Coincident(g5,g6)
    c: Vertical(g6)
    c: Coincident(g6,g7)
    c: Horizontal(g7)
    c: Coincident(g7,g8)
    c: Vertical(g8)
    c: Coincident(g8,g9)
    c: Horizontal(g9)
    c: Horizontal(g10)
    c: Coincident(g10,g11)
    c: Vertical(g11)
    c: Coincident(g5,g11)
    c: Coincident(g12,g9)
    c: Vertical(g12)
    c: Coincident(g13,g0)
    c: Vertical(g13)
    c: Coincident(g10,g13)
    c: Equal(g13,g12)
    c: Distance(g13) = 2
    c: Equal(g10,g9)
    c: Distance(g10) = 5
    c: DistanceX(g1,g2) = 0
    c: Symmetric(g0,g4,g-1)
    c: Equal(g8,g11)
    c: Distance(g11) = 4
    c: Distance(g5) = 5
    c: DistanceY(g4,g0) = 24
    c: DistanceX(g1) = 36
    c: Horizontal(g16)
    c: Coincident(g15,g16)
    c: Perpendicular(g15,g16)
    c: Perpendicular(g14,g16)
    c: Coincident(g17,g14)
    c: Horizontal(g17)
    c: Coincident(g18,g15)
    c: Horizontal(g18)
    c: Tangent(g15,g18)
    c: Tangent(g17,g14)
    c: Coincident(g17,g12)
    c: Coincident(g18,g4)
    c: Equal(g14,g15)
    c: Equal(g7,g5)
    c: Distance(g16) = 34
    c: Equal(g8,g11)
    c: Equal(g12,g13)
    c: Coincident(g14,g16)
    c: Equal(g18,g17)
    c: Radius(g15) = 8
FEATURE [PartDesign::Pad] Pad012
  Length = 33
  Length2 = 100
  Reversed = true
  Sketch = -> Sketch019
  Type = 0
FEATURE [Sketcher::SketchObject] Sketch020
  sketch-geometry (3):
    g0: ArcOfCircle CenterX=0 CenterY=46.3048 CenterZ=0 NormalX=0 NormalY=0 NormalZ=1 Radius=70.3048 StartAngle=3.86059 EndAngle=4.71239
    g1: LineSegment StartX=-52.9021 StartY=0 StartZ=0 EndX=0 EndY=0 EndZ=0
    g2: LineSegment StartX=0 StartY=0 StartZ=0 EndX=0 EndY=-24 EndZ=0
  constraints (9):
    c: Distance(g1) = 52.9021
    c: Distance(g2) = 24
    c: Coincident(g0,g2)
    c: Coincident(g0,g1)
    c: Coincident(g1,g2)
    c: Coincident(g1,g-1)
    c: Vertical(g2)
    c: Horizontal(g1)
    c: Perpendicular(g0,g2)
FEATURE [PartDesign::Revolution] Revolution002
  Angle = 360
  Axis = (0,1,0)
  Base = (0,0,0)
  ReferenceAxis = -> Sketch020 [V_Axis]
  Sketch = -> Sketch020
FEATURE [Part::MultiCommon] Common
  Shapes = -> [Pad012,Revolution002]
FEATURE [Part::Cut] Cut112
  Base = -> Common
  Tool = -> Revolution001
FEATURE [Part::MultiFuse] Fusion065
  Shapes = -> [Revolution,Cut112]
FEATURE [Sketcher::SketchObject] Sketch021
  Placement = pos=(0,0,0) rot=(1,0,0;1.5708rad)
  sketch-geometry (6):
    g0: ArcOfCircle CenterX=-5 CenterY=0 CenterZ=0 NormalX=0 NormalY=0 NormalZ=1 Radius=4 StartAngle=1.5708 EndAngle=4.71239
    g1: ArcOfCircle CenterX=5 CenterY=0 CenterZ=0 NormalX=0 NormalY=0 NormalZ=1 Radius=4 StartAngle=4.71239 EndAngle=7.85398
    g2: LineSegment StartX=-5 StartY=-4 StartZ=0 EndX=5 EndY=-4 EndZ=0
    g3: LineSegment StartX=-5 StartY=4 StartZ=0 EndX=5 EndY=4 EndZ=0
    g4: Circle CenterX=-5 CenterY=0 CenterZ=0 NormalX=0 NormalY=0 NormalZ=1 Radius=1.4
    g5: Circle CenterX=5 CenterY=0 CenterZ=0 NormalX=0 NormalY=0 NormalZ=1 Radius=1.4
  constraints (14):
    c: Tangent(g0,g3) = 1.5708
    c: Tangent(g0,g2) = -1.5708
    c: Tangent(g2,g1) = -1.5708
    c: Tangent(g3,g1) = 1.5708
    c: Horizontal(g2)
    c: Equal(g0,g1)
    c: PointOnObject(g0,g-1)
    c: Coincident(g4,g0)
    c: Coincident(g5,g1)
    c: Radius(g5) = 1.4
    c: Equal(g5,g4)
    c: Radius(g1) = 4
    c: Symmetric(g0,g1,g-2)
    c: Distance(g3) = 10
FEATURE [PartDesign::Pad] Pad013
  Length = 20
  Length2 = 100
  Placement = pos=(0,0,0) rot=(1,0,0;1.5708rad)
  Sketch = -> Sketch021
  Type = 0
FEATURE [Part::MultiFuse] Fusion066
  Shapes = -> [Fusion065,Pad013]
FEATURE [Part::Fillet] Fillet018013009
  Base = -> Fusion066
  Edges = 1 edges r=10: [Edge9]
  Placement = pos=(20,118,59) rot=(0,0,1;3.14159rad)
FEATURE [Sketcher::SketchObject] Sketch022
  Placement = pos=(20,183,59) rot=(1,0,0;1.5708rad)
  sketch-geometry (2):
    g0: Circle CenterX=5 CenterY=0 CenterZ=0 NormalX=0 NormalY=0 NormalZ=1 Radius=1.5
    g1: Circle CenterX=-5 CenterY=0 CenterZ=0 NormalX=0 NormalY=0 NormalZ=1 Radius=1.5
  constraints (2):
    c: Radius(g1) = 1.5
    c: Equal(g1,g0)
FEATURE [PartDesign::Pad] Pad014
  Length = 100
  Length2 = 100
  Placement = pos=(20,183,59) rot=(0,0,1;3.14159rad)
  Sketch = -> Sketch022
  Type = 0
FEATURE [Part::Cut] Cut113
  Base = -> Clone013
  Tool = -> Pad014
FEATURE [Part::MultiFuse] Fusion067
  Shapes = -> [Part__Mirroring007010,Chamfer115]
FEATURE [Part::Box] Box066  label="Cubo016"
  Height = 19
  Length = 129
  Placement = pos=(-2,20,72) rot=(0,0,1;0rad)
  Width = 32
FEATURE [Part::Cut] Cut114
  Base = -> Chamfer102
  Tool = -> Box066
FEATURE [Part::FeaturePython] Clone027  label="Clone of Cut080026091"  # WARN: FeaturePython — macro-defined, semantics opaque (R4)
  Placement = pos=(20.8,4,-65) rot=(0,0,-1;1.5708rad)
  Scale = (1,1,1)
FEATURE [Part::Box] Box067  label="Cubo017"
  Height = 26
  Length = 101
  Placement = pos=(-48,13,154) rot=(0,0,1;0rad)
  Width = 46
FEATURE [Part::Cut] Cut115
  Base = -> Clone027
  Tool = -> Box067
FEATURE [Part::Box] Box068  label="Cubo018"
  Height = 34
  Length = 46
  Placement = pos=(-44,13,129) rot=(0,0,1;0rad)
  Width = 46
FEATURE [Part::Cut] Cut116
  Base = -> Cut115
  Tool = -> Box068
FEATURE [Part::Box] Box069  label="Cubo019"
  Height = 34
  Length = 46
  Placement = pos=(2,13,154) rot=(0,0,1;0rad)
  Width = 46
FEATURE [Part::MultiFuse] Fusion068
  Shapes = -> [Cut116,Box069]
FEATURE [Part::Box] Box070  label="Cubo020"
  Height = 76
  Length = 46
  Placement = pos=(145,-48,0) rot=(0,0,1;0rad)
  Width = 46
FEATURE [Part::Chamfer] Chamfer116
  Base = -> Box070
  Edges = 12 edges r=4: [Edge1,Edge2,Edge3,Edge4,Edge5,Edge6,Edge7,Edge8,Edge9,Edge10,Edge11,Edge12]
FEATURE [Part::Box] Box071  label="Cubo021"
  Height = 25
  Length = 56
  Placement = pos=(140,-53,-3) rot=(0,0,1;0rad)
  Width = 56
FEATURE [Part::Chamfer] Chamfer117
  Base = -> Box071
  Edges = 8 edges r=2: [Edge1,Edge2,Edge3,Edge5,Edge6,Edge7,Edge10,Edge12]
FEATURE [Part::MultiFuse] Fusion069
  Placement = pos=(58,61,5) rot=(0,-1,0;1.5708rad)
  Shapes = -> [Chamfer116,Chamfer117]
FEATURE [Sketcher::SketchObject] Sketch023
  ExternalGeometry = -> [Fusion069]
  Placement = pos=(61,61,5) rot=(0.707107,0,0.707107;3.14159rad)
  Support = -> Fusion069 [Face32]
  sketch-geometry (4):
    g0: LineSegment StartX=150 StartY=43 StartZ=0 EndX=186 EndY=43 EndZ=0
    g1: LineSegment StartX=186 StartY=43 StartZ=0 EndX=186 EndY=7 EndZ=0
    g2: LineSegment StartX=186 StartY=7 StartZ=0 EndX=150 EndY=7 EndZ=0
    g3: LineSegment StartX=150 StartY=7 StartZ=0 EndX=150 EndY=43 EndZ=0
  constraints (12):
    c: Coincident(g0,g1)
    c: Coincident(g1,g2)
    c: Coincident(g2,g3)
    c: Coincident(g3,g0)
    c: Horizontal(g0)
    c: Horizontal(g2)
    c: Vertical(g1)
    c: Vertical(g3)
    c: Equal(g1,g0)
    c: Distance(g2,g-6) = 10
    c: Distance(g0,g-4) = 10
    c: Distance(g0,g-3) = 10
FEATURE [PartDesign::Pocket] Pocket005
  Length = 10
  Placement = pos=(58,61,5) rot=(0,-1,0;1.5708rad)
  Sketch = -> Sketch023
  Type = 0
FEATURE [PartDesign::Chamfer] Chamfer118
  Base = -> Pocket005 [Edge79,Edge77,Edge73,Edge74,Edge75,Edge76,Edge83,Edge81]
  Placement = pos=(58,61,5) rot=(0,-1,0;1.5708rad)
  Size = 4
FEATURE [PartDesign::Chamfer] Chamfer119
  Base = -> Chamfer118 [Edge15,Edge14,Edge10,Edge11]
  Placement = pos=(58,61,5) rot=(0,-1,0;1.5708rad)
  Size = 5
FEATURE [Part::Torus] Torus  label="Toro"
  Angle1 = -180
  Angle2 = 180
  Angle3 = 360
  Placement = pos=(51,35.5,173.5) rot=(0,1,0;1.5708rad)
  Radius1 = 10
  Radius2 = 4
FEATURE [Part::MultiFuse] Fusion070
  Shapes = -> [Chamfer119,Torus]
FEATURE [PartDesign::Fillet] Fillet002
  Base = -> Fusion070 [Edge115]
  Radius = 10
FEATURE [Part::MultiFuse] Fusion071
  Shapes = -> [Fusion068,Fillet002]
FEATURE [Part::Cylinder] Cylinder082  label="Cilindro023"
  Angle = 360
  Height = 36
  Placement = pos=(33.8,54,137) rot=(1,0,0;1.5708rad)
  Radius = 12
FEATURE [Part::Cut] Cut117
  Base = -> Fusion071
  Tool = -> Cylinder082
